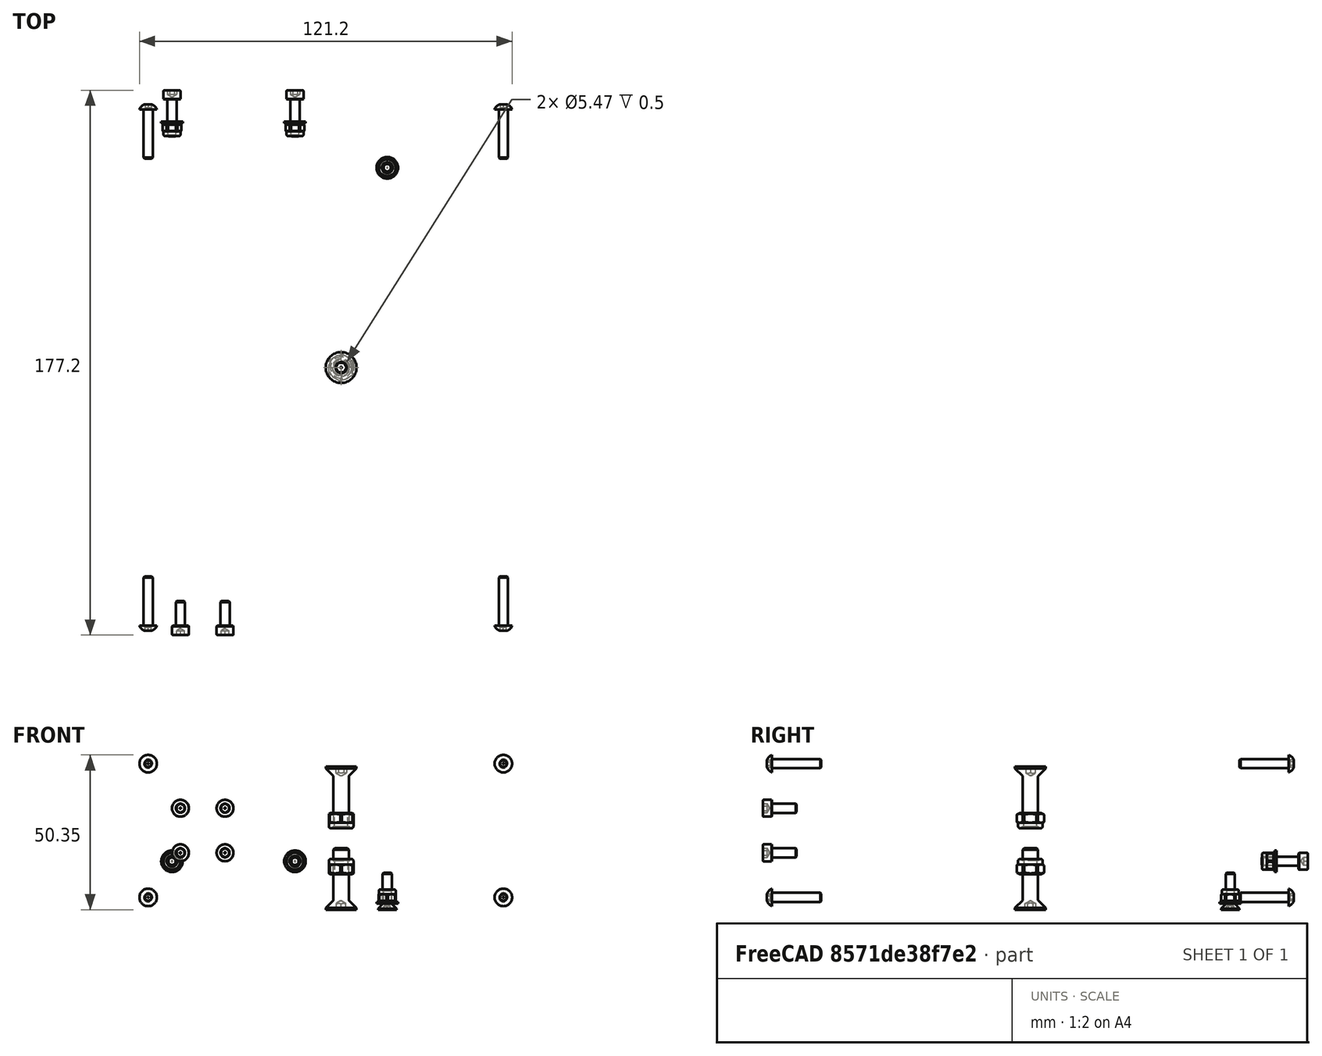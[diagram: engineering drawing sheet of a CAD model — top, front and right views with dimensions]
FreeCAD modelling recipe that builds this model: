
FCSTD DOCUMENT  (FreeCAD 0.20R28730 (Git))
Label: OpenSolder Station
License: All rights reserved
LicenseURL: http://en.wikipedia.org/wiki/All_rights_reserved
objects: Part::FeaturePython×25, TechDraw::DrawViewBalloon×24, App::Link×20, App::DocumentObjectGroup×13, TechDraw::DrawViewDimension×9, PartDesign::CoordinateSystem×7, TechDraw::DrawProjGroupItem×5, Spreadsheet::Sheet×4, TechDraw::DrawSVGTemplate×4, TechDraw::DrawPage×4, Sketcher::SketchObject×3, TechDraw::DrawProjGroup×2, TechDraw::DrawViewPart×2, App::FeaturePython×1, App::Part×1, TechDraw::DrawViewSpreadsheet×1, TechDraw::DrawViewSection×1
note: 35 computed .brp shape members not serialized (recipe doc carries the construction recipe); baked Part::Feature solids carry a one-line shape summary decoded from their .brp
EXTERNAL_REF file=Parts/Enclosure 1455Q1602BK.FCStd obj=LCS_Extrusion
EXTERNAL_REF file=Parts/Enclosure 1455Q1602BK.FCStd obj=Body
EXTERNAL_REF file=Parts/Enclosure 1455Q1602BK.FCStd obj=LCS_Cap
EXTERNAL_REF file=Parts/Enclosure 1455Q1602BK.FCStd obj=Body001
EXTERNAL_REF file=Parts/Enclosure 1455Q1602BK.FCStd obj=LCS_Transformer_Mounting_Hole
EXTERNAL_REF file=Parts/Transformer Spacer.FCStd obj=LCS_Transformer_Spacer_2
EXTERNAL_REF file=Parts/Transformer Spacer.FCStd obj=Body
EXTERNAL_REF file=Parts/Enclosure 1455Q1602BK.FCStd obj=LCS_Transformer_Outside_Mounting_Hole
EXTERNAL_REF file=Parts/Transformer Spacer.FCStd obj=LCS_Transformer_Spacer_Nut_Bottom
EXTERNAL_REF file=Parts/Transformer Spacer.FCStd obj=LCS_Transformer_Spacer_Nut_Top
EXTERNAL_REF file=Parts/Transformer.FCStd obj=LCS_Foam_Bottom
EXTERNAL_REF file=Parts/Transformer.FCStd obj=Body001
EXTERNAL_REF file=Parts/Transformer.FCStd obj=LCS_Foam_Top
EXTERNAL_REF file=Parts/Transformer.FCStd obj=LCS_Transformer_Bottom
EXTERNAL_REF file=Parts/Transformer.FCStd obj=Body
EXTERNAL_REF file=Parts/Transformer.FCStd obj=LCS_Transformer_Top
EXTERNAL_REF file=Parts/Transformer.FCStd obj=LCS_Transformer_Washer_Plane
EXTERNAL_REF file=Parts/Transformer.FCStd obj=Body002
EXTERNAL_REF file=Parts/Transformer.FCStd obj=LCS_Transformer_Washer_Screw_Top
EXTERNAL_REF file=Parts/Panels.FCStd obj=LCS_Front_Hole_1_Bottom
EXTERNAL_REF file=Parts/Panels.FCStd obj=Body
EXTERNAL_REF file=Parts/Panels.FCStd obj=LCS_Rear_Hole_1_Bottom
EXTERNAL_REF file=Parts/Panels.FCStd obj=Body001
EXTERNAL_REF file=Parts/PCB.FCStd obj=LCS_PCBA
EXTERNAL_REF file=Parts/Panels.FCStd obj=LCS_PCBA_Mount
EXTERNAL_REF file=Parts/PCB.FCStd obj=openSolderV0_2_1
EXTERNAL_REF file=Parts/Connector Minijack MJ-064H.FCStd obj=LCS_1
EXTERNAL_REF file=Parts/Panels.FCStd obj=LCS_Rear_Holder_Connector
EXTERNAL_REF file=Parts/Connector Minijack MJ-064H.FCStd obj=Body
EXTERNAL_REF file=Parts/Panels.FCStd obj=LCS_Rear_STlink_Connector
EXTERNAL_REF file=Parts/Connector IEC-C14 703W-0004.FCStd obj=LCS_IEC_Connector
EXTERNAL_REF file=Parts/Panels.FCStd obj=LCS_Rear_IDC_Connector
EXTERNAL_REF file=Parts/Connector IEC-C14 703W-0004.FCStd obj=_03W_00____04
EXTERNAL_REF file=Parts/Panels.FCStd obj=LCS_Rear_Switch
EXTERNAL_REF file=Parts/Rocker Switch CWSB11AA2F.FCStd obj=LCS_Switch
EXTERNAL_REF file=Parts/Rocker Switch CWSB11AA2F.FCStd obj=CWSB11AA2F
EXTERNAL_REF file=Parts/Rotary Encoder Knob.FCStd obj=LCS_Knob
EXTERNAL_REF file=Parts/Rotary Encoder Knob.FCStd obj=Body
EXTERNAL_REF file=Parts/Panels.FCStd obj=LCS_Front_Connector_Hole_1
EXTERNAL_REF file=Parts/Panels.FCStd obj=LCS_Front_Connector_Hole_2
EXTERNAL_REF file=Parts/Panels.FCStd obj=LCS_Front_Connector_Hole_3
EXTERNAL_REF file=Parts/Panels.FCStd obj=LCS_Front_Connector_Hole_4
EXTERNAL_REF file=Parts/Panels.FCStd obj=LCS_Front_Hole_1_Top
EXTERNAL_REF file=Parts/Panels.FCStd obj=LCS_Front_Hole_2_Top
EXTERNAL_REF file=Parts/Panels.FCStd obj=LCS_Front_Hole_3_Top
EXTERNAL_REF file=Parts/Panels.FCStd obj=LCS_Front_Hole_4_Top
EXTERNAL_REF file=Parts/Panels.FCStd obj=LCS_Rear_Hole_4_Top
EXTERNAL_REF file=Parts/Panels.FCStd obj=LCS_Rear_Hole_1_Top
EXTERNAL_REF file=Parts/Panels.FCStd obj=LCS_Rear_Hole_2_Top
EXTERNAL_REF file=Parts/Panels.FCStd obj=LCS_Rear_Hole_3_Top
EXTERNAL_REF file=Parts/Enclosure 1455Q1602BK.FCStd obj=LCS_Outside_Grounding_Hole
EXTERNAL_REF file=Parts/Connector IEC-C14 703W-0004.FCStd obj=LCS_IEC_Hole_1
EXTERNAL_REF file=Parts/Connector IEC-C14 703W-0004.FCStd obj=LCS_IEC_Hole_2
EXTERNAL_REF file=Parts/Enclosure 1455Q1602BK.FCStd obj=LCS_Grounding_Hole
EXTERNAL_REF file=Parts/Rubber Pad.FCStd obj=LCS_1
EXTERNAL_REF file=Parts/Rubber Pad.FCStd obj=Body
EXTERNAL_REF file=Parts/Fuse Holder Inline.FCStd obj=LCS_0
EXTERNAL_REF file=Parts/Fuse Holder Inline.FCStd obj=Fuse_Holder_01500274ZXU

FEATURE [PartDesign::CoordinateSystem] LCS_Origin
  AttacherType = Attacher::AttachEngine3D
  MapMode = 2
  Support = -> [X_Axis]
FEATURE [App::FeaturePython] Variables  # WARN: FeaturePython — macro-defined, semantics opaque (R4)
  Type = App::PropertyContainer
FEATURE [App::DocumentObjectGroup] Constraints
FEATURE [App::Link] _455Q1602BK_Extrusion  label="Enclosure_1455Q1602BK_Extrusion"
  AssemblyType = Part::Link
  AttachedBy = #LCS_Extrusion
  AttachedTo = Parent Assembly#LCS_Origin
  AttachmentOffset = pos=(0,0,0) rot=(-1,0,0;1.5708rad)
  LinkPlacement = pos=(0,0,0) rot=(-1,0,0;1.5708rad)
  LinkedObject = -> <external Parts/Enclosure 1455Q1602BK.FCStd>#Body
  Placement = pos=(0,0,0) rot=(-1,0,0;1.5708rad)
  SolverId = Asm4EE
  expr: Placement = LCS_Origin.Placement * AttachmentOffset * Enclosure_1455Q1602BK#LCS_Extrusion.Placement ^ -1
FEATURE [App::Link] _455Q1602BK_Cap  label="Enclosure_1455Q1602BK_Cap"
  AssemblyType = Part::Link
  AttachedBy = #LCS_Cap
  AttachedTo = _455Q1602BK_Extrusion#LCS_Extrusion
  LinkPlacement = pos=(0,2.29e-14,51.5) rot=(-1,0,0;1.5708rad)
  LinkedObject = -> <external Parts/Enclosure 1455Q1602BK.FCStd>#Body001
  Placement = pos=(0,2.29e-14,51.5) rot=(-1,0,0;1.5708rad)
  SolverId = Asm4EE
  expr: Placement = _455Q1602BK_Extrusion.Placement * Enclosure_1455Q1602BK#LCS_Extrusion.Placement * AttachmentOffset * Enclosure_1455Q1602BK#LCS_Cap.Placement ^ -1
FEATURE [App::Link] Transformer_Spacer
  AssemblyType = Part::Link
  AttachedBy = #LCS_Transformer_Spacer_2
  AttachedTo = _455Q1602BK_Extrusion#LCS_Transformer_Mounting_Hole
  AttachmentOffset = pos=(0,0,0) rot=(0,0,-1;1.5708rad)
  LinkPlacement = pos=(5,1.2e-14,21.5) rot=(0,0,-1;1.5708rad)
  LinkedObject = -> <external Parts/Transformer Spacer.FCStd>#Body
  Placement = pos=(5,1.2e-14,21.5) rot=(0,0,-1;1.5708rad)
  SolverId = Asm4EE
  expr: Placement = _455Q1602BK_Extrusion.Placement * Enclosure_1455Q1602BK#LCS_Transformer_Mounting_Hole.Placement * AttachmentOffset * Transformer_Spacer#LCS_Transformer_Spacer_2.Placement ^ -1
FEATURE [Part::FeaturePython] Screw  label="M5x20-Screw"  # Fasteners workbench fastener (typed FeaturePython)
  AssemblyType = Part::Link
  AttachedBy = Origin
  AttachedTo = _455Q1602BK_Extrusion#LCS_Transformer_Outside_Mounting_Hole
  Placement = pos=(5,0,0) rot=(0.707107,-0.707107,0;3.14159rad)
  SolverId = Asm4EE
  diameter = 5
  invert = false
  length = 4
  lengthCustom = 20
  matchOuter = false
  offset = 0
  thread = false
  type = 18
  expr: Placement = _455Q1602BK_Extrusion.Placement * Enclosure_1455Q1602BK#LCS_Transformer_Outside_Mounting_Hole.Placement * AttachmentOffset
FEATURE [Part::FeaturePython] Nut  label="M5-Nut001"  # Fasteners workbench fastener (typed FeaturePython)
  AssemblyType = Part::Link
  AttachedBy = Origin
  AttachedTo = Transformer_Spacer#LCS_Transformer_Spacer_Nut_Bottom
  AttachmentOffset = pos=(0,0,0) rot=(0,0,1;1.5708rad)
  Placement = pos=(5,6.5e-15,11.5) rot=(0,0,1;1.5708rad)
  SolverId = Asm4EE
  diameter = 3
  invert = false
  matchOuter = false
  offset = 0
  thread = false
  type = 5
  expr: Placement = Transformer_Spacer.Placement * Transformer_Spacer#LCS_Transformer_Spacer_Nut_Bottom.Placement * AttachmentOffset
FEATURE [Part::FeaturePython] Nut001  label="M5-Nut"  # Fasteners workbench fastener (typed FeaturePython)
  AssemblyType = Part::Link
  AttachedBy = Origin
  AttachedTo = Transformer_Spacer#LCS_Transformer_Spacer_Nut_Top
  AttachmentOffset = pos=(0,0,0) rot=(0.707107,-0.707107,0;3.14159rad)
  Placement = pos=(5,1.75e-14,31.5) rot=(0.707107,-0.707107,0;3.14159rad)
  SolverId = Asm4EE
  diameter = 3
  invert = false
  matchOuter = false
  offset = 0
  thread = false
  type = 5
  expr: Placement = Transformer_Spacer.Placement * Transformer_Spacer#LCS_Transformer_Spacer_Nut_Top.Placement * AttachmentOffset
FEATURE [App::Link] Foam_Bottom
  AssemblyType = Part::Link
  AttachedBy = #LCS_Foam_Bottom
  AttachedTo = _455Q1602BK_Extrusion#LCS_Transformer_Mounting_Hole
  AttachmentOffset = pos=(0,0,0) rot=(1,0,0;3.14159rad)
  LinkPlacement = pos=(5,1.3e-15,2) rot=(0,0,1;3.14159rad)
  LinkedObject = -> <external Parts/Transformer.FCStd>#Body001
  Placement = pos=(5,1.3e-15,2) rot=(0,0,1;3.14159rad)
  SolverId = Asm4EE
  expr: Placement = _455Q1602BK_Extrusion.Placement * Enclosure_1455Q1602BK#LCS_Transformer_Mounting_Hole.Placement * AttachmentOffset * Transformer#LCS_Foam_Bottom.Placement ^ -1
FEATURE [App::Link] Transformer
  AssemblyType = Part::Link
  AttachedBy = #LCS_Transformer_Bottom
  AttachedTo = Foam_Bottom#LCS_Foam_Top
  AttachmentOffset = pos=(0,0,0) rot=(0,0,-1;1.5708rad)
  LinkPlacement = pos=(5,-2.2e-15,2) rot=(0,0,1;4.71239rad)
  LinkedObject = -> <external Parts/Transformer.FCStd>#Body
  Placement = pos=(5,-2.2e-15,2) rot=(0,0,1;4.71239rad)
  SolverId = Asm4EE
  expr: Placement = Foam_Bottom.Placement * Transformer#LCS_Foam_Top.Placement * AttachmentOffset * Transformer#LCS_Transformer_Bottom.Placement ^ -1
FEATURE [App::Link] Foam_Top
  AssemblyType = Part::Link
  AttachedBy = #LCS_Foam_Bottom
  AttachedTo = Transformer#LCS_Transformer_Top
  LinkPlacement = pos=(5,2.42e-14,47.5) rot=(0,0,1;4.71239rad)
  LinkedObject = -> <external Parts/Transformer.FCStd>#Body001
  Placement = pos=(5,2.42e-14,47.5) rot=(0,0,1;4.71239rad)
  SolverId = Asm4EE
  expr: Placement = Transformer.Placement * Transformer#LCS_Transformer_Top.Placement * AttachmentOffset * Transformer#LCS_Foam_Bottom.Placement ^ -1
FEATURE [App::Link] Transformer_Washer
  AssemblyType = Part::Link
  AttachedBy = #LCS_Transformer_Washer_Plane
  AttachedTo = Foam_Top#LCS_Foam_Top
  LinkPlacement = pos=(5,2.29e-14,43) rot=(0,0,1;4.71239rad)
  LinkedObject = -> <external Parts/Transformer.FCStd>#Body002
  Placement = pos=(5,2.29e-14,43) rot=(0,0,1;4.71239rad)
  SolverId = Asm4EE
  expr: Placement = Foam_Top.Placement * Transformer#LCS_Foam_Top.Placement * AttachmentOffset * Transformer#LCS_Transformer_Washer_Plane.Placement ^ -1
FEATURE [App::DocumentObjectGroup] Transformer_Group
  Group = -> [Foam_Bottom,Transformer,Foam_Top,Transformer_Washer]
FEATURE [Part::FeaturePython] Screw001  label="M5x20-Screw001"  # Fasteners workbench fastener (typed FeaturePython)
  AssemblyType = Part::Link
  AttachedBy = Origin
  AttachedTo = Transformer_Washer#LCS_Transformer_Washer_Screw_Top
  AttachmentOffset = pos=(0,0,-2) rot=(1,0,0;3.14159rad)
  Placement = pos=(5,2.37e-14,46.5) rot=(0,0,-1;3.14159rad)
  SolverId = Asm4EE
  diameter = 5
  invert = false
  length = 4
  lengthCustom = 20
  matchOuter = false
  offset = 0
  thread = false
  type = 18
  expr: Placement = Transformer_Washer.Placement * Transformer#LCS_Transformer_Washer_Screw_Top.Placement * AttachmentOffset
FEATURE [App::DocumentObjectGroup] Transformer_Fasteners
  Group = -> [Screw,Screw001,Nut001,Nut]
FEATURE [Sketcher::SketchObject] Front_Panel_Sketch
  AttachmentOffset = pos=(0,0,80) rot=(0,0,1;0rad)
  FullyConstrained = true
  MapMode = 5
  Placement = pos=(0,-80,-1.78e-14) rot=(1,0,0;1.5708rad)
  Support = -> [XZ_Plane]
  sketch-geometry (8):
    g0: LineSegment StartX=-57.75 StartY=47.5 StartZ=0 EndX=57.75 EndY=47.5 EndZ=0
    g1: LineSegment StartX=57.75 StartY=47.5 StartZ=0 EndX=57.75 EndY=4 EndZ=0
    g2: LineSegment StartX=57.75 StartY=4 StartZ=0 EndX=-57.75 EndY=4 EndZ=0
    g3: LineSegment StartX=-57.75 StartY=4 StartZ=0 EndX=-57.75 EndY=47.5 EndZ=0
    g4: Circle CenterX=-57.75 CenterY=47.5 CenterZ=0 NormalX=0 NormalY=0 NormalZ=1 AngleXU=0 Radius=1.75
    g5: Circle CenterX=57.75 CenterY=47.5 CenterZ=0 NormalX=0 NormalY=0 NormalZ=1 AngleXU=0 Radius=1.75
    g6: Circle CenterX=57.75 CenterY=4 CenterZ=0 NormalX=0 NormalY=0 NormalZ=1 AngleXU=0 Radius=1.75
    g7: Circle CenterX=-57.75 CenterY=4 CenterZ=0 NormalX=0 NormalY=0 NormalZ=1 AngleXU=0 Radius=1.75
  constraints (19):
    c: Coincident(g0,g1)
    c: Coincident(g1,g2)
    c: Coincident(g2,g3)
    c: Coincident(g3,g0)
    c: Horizontal(g0)
    c: Vertical(g1)
    c: Vertical(g3)
    c: Symmetric(g2,g1,g-2)
    c: DistanceX(g2,g2) = 115.5
    c: DistanceY(g3,g3) = 43.5
    c: DistanceY(g-1,g2) = 4
    c: Coincident(g4,g0)
    c: Coincident(g5,g0)
    c: Coincident(g6,g1)
    c: Coincident(g7,g2)
    c: Equal(g7,g4)
    c: Equal(g7,g5)
    c: Equal(g7,g6)
    c: Diameter(g7) = 3.5
FEATURE [Sketcher::SketchObject] Front_Panel_Sketch001  label="Rear_Panel_Sketch"
  AttachmentOffset = pos=(0,0,-80) rot=(0,0,1;0rad)
  FullyConstrained = true
  MapMode = 5
  Placement = pos=(0,80,1.78e-14) rot=(1,0,0;1.5708rad)
  Support = -> [XZ_Plane]
  sketch-geometry (8):
    g0: LineSegment StartX=-57.75 StartY=47.5 StartZ=0 EndX=57.75 EndY=47.5 EndZ=0
    g1: LineSegment StartX=57.75 StartY=47.5 StartZ=0 EndX=57.75 EndY=4 EndZ=0
    g2: LineSegment StartX=57.75 StartY=4 StartZ=0 EndX=-57.75 EndY=4 EndZ=0
    g3: LineSegment StartX=-57.75 StartY=4 StartZ=0 EndX=-57.75 EndY=47.5 EndZ=0
    g4: Circle CenterX=-57.75 CenterY=47.5 CenterZ=0 NormalX=0 NormalY=0 NormalZ=1 AngleXU=0 Radius=1.75
    g5: Circle CenterX=57.75 CenterY=47.5 CenterZ=0 NormalX=0 NormalY=0 NormalZ=1 AngleXU=0 Radius=1.75
    g6: Circle CenterX=57.75 CenterY=4 CenterZ=0 NormalX=0 NormalY=0 NormalZ=1 AngleXU=0 Radius=1.75
    g7: Circle CenterX=-57.75 CenterY=4 CenterZ=0 NormalX=0 NormalY=0 NormalZ=1 AngleXU=0 Radius=1.75
  constraints (19):
    c: Coincident(g0,g1)
    c: Coincident(g1,g2)
    c: Coincident(g2,g3)
    c: Coincident(g3,g0)
    c: Horizontal(g0)
    c: Vertical(g1)
    c: Vertical(g3)
    c: Symmetric(g2,g1,g-2)
    c: DistanceX(g2,g2) = 115.5
    c: DistanceY(g3,g3) = 43.5
    c: DistanceY(g-1,g2) = 4
    c: Coincident(g4,g0)
    c: Coincident(g5,g0)
    c: Coincident(g6,g1)
    c: Coincident(g7,g2)
    c: Equal(g7,g4)
    c: Equal(g7,g5)
    c: Equal(g7,g6)
    c: Diameter(g7) = 3.5
FEATURE [PartDesign::CoordinateSystem] LCS_Assembly_Front_Hole
  AttacherType = Attacher::AttachEngine3D
  MapMode = 11
  Placement = pos=(-57.75,-80,47.5) rot=(0.57735,-0.57735,0.57735;2.0944rad)
  Support = -> [Front_Panel_Sketch]
FEATURE [PartDesign::CoordinateSystem] LCS_Assembly_Rear_Hole
  AttacherType = Attacher::AttachEngine3D
  MapMode = 11
  Placement = pos=(57.75,80,47.5) rot=(0.57735,-0.57735,0.57735;2.0944rad)
  Support = -> [Front_Panel_Sketch001]
FEATURE [App::Link] Front_Panel
  AssemblyType = Part::Link
  AttachedBy = #LCS_Front_Hole_1_Bottom
  AttachedTo = Parent Assembly#LCS_Assembly_Front_Hole
  LinkPlacement = pos=(0,-80,25.75) rot=(0,0,1;0rad)
  LinkedObject = -> <external Parts/Panels.FCStd>#Body
  Placement = pos=(0,-80,25.75) rot=(0,0,1;0rad)
  SolverId = Asm4EE
  expr: Placement = LCS_Assembly_Front_Hole.Placement * AttachmentOffset * Panels#LCS_Front_Hole_1_Bottom.Placement ^ -1
FEATURE [App::Link] Rear_Panel
  AssemblyType = Part::Link
  AttachedBy = #LCS_Rear_Hole_1_Bottom
  AttachedTo = Parent Assembly#LCS_Assembly_Rear_Hole
  AttachmentOffset = pos=(0,0,0) rot=(1,0,0;3.14159rad)
  LinkPlacement = pos=(-7.1e-15,80,25.75) rot=(0,0,1;3.14159rad)
  LinkedObject = -> <external Parts/Panels.FCStd>#Body001
  Placement = pos=(-7.1e-15,80,25.75) rot=(0,0,1;3.14159rad)
  SolverId = Asm4EE
  expr: Placement = LCS_Assembly_Rear_Hole.Placement * AttachmentOffset * Panels#LCS_Rear_Hole_1_Bottom.Placement ^ -1
FEATURE [App::Link] openSolderV0_2_PCBA  label="openSolderV0.2_PCBA"
  AssemblyType = Part::Link
  AttachedBy = #LCS_PCBA
  AttachedTo = Front_Panel#LCS_PCBA_Mount
  AttachmentOffset = pos=(0,0,0) rot=(1,0,0;3.14159rad)
  LinkPlacement = pos=(0,-73,25.75) rot=(0,0.707107,0.707107;3.14159rad)
  LinkedObject = -> <external Parts/PCB.FCStd>#openSolderV0_2_1
  Placement = pos=(0,-73,25.75) rot=(0,0.707107,0.707107;3.14159rad)
  SolverId = Asm4EE
  expr: Placement = Front_Panel.Placement * Panels#LCS_PCBA_Mount.Placement * AttachmentOffset * PCB#LCS_PCBA.Placement ^ -1
FEATURE [App::Link] Connector_Holder
  AssemblyType = Part::Link
  AttachedBy = #LCS_1
  AttachedTo = Rear_Panel#LCS_Rear_Holder_Connector
  AttachmentOffset = pos=(0,0,0) rot=(0,0,1;1.5708rad)
  LinkPlacement = pos=(47.5,84,10.75) rot=(0,0,1;4.71239rad)
  LinkedObject = -> <external Parts/Connector Minijack MJ-064H.FCStd>#Body
  Placement = pos=(47.5,84,10.75) rot=(0,0,1;4.71239rad)
  SolverId = Asm4EE
  expr: Placement = Rear_Panel.Placement * Panels#LCS_Rear_Holder_Connector.Placement * AttachmentOffset * Connector_Minijack_MJ_064H#LCS_1.Placement ^ -1
FEATURE [App::Link] Connector_STlink
  AssemblyType = Part::Link
  AttachedBy = #LCS_1
  AttachedTo = Rear_Panel#LCS_Rear_STlink_Connector
  AttachmentOffset = pos=(0,0,0) rot=(0,0,1;1.5708rad)
  LinkPlacement = pos=(47.5,84,40.75) rot=(0,0,1;4.71239rad)
  LinkedObject = -> <external Parts/Connector Minijack MJ-064H.FCStd>#Body
  Placement = pos=(47.5,84,40.75) rot=(0,0,1;4.71239rad)
  SolverId = Asm4EE
  expr: Placement = Rear_Panel.Placement * Panels#LCS_Rear_STlink_Connector.Placement * AttachmentOffset * Connector_Minijack_MJ_064H#LCS_1.Placement ^ -1
FEATURE [App::Link] _03W_00_IEC_C14_Connector  label="Connector_IEC-C14_703W-0004"
  AssemblyType = Part::Link
  AttachedBy = #LCS_IEC_Connector
  AttachedTo = Rear_Panel#LCS_Rear_IDC_Connector
  AttachmentOffset = pos=(0,0,0) rot=(0,0,1;1.5708rad)
  LinkPlacement = pos=(-27.5841,83.3477,15.75) rot=(0,1,0;3.14159rad)
  LinkedObject = -> <external Parts/Connector IEC-C14 703W-0004.FCStd>#_03W_00____04
  Placement = pos=(-27.5841,83.3477,15.75) rot=(0,1,0;3.14159rad)
  SolverId = Asm4EE
  expr: Placement = Rear_Panel.Placement * Panels#LCS_Rear_IDC_Connector.Placement * AttachmentOffset * Connector_IEC_C14_703W_0004#LCS_IEC_Connector.Placement ^ -1
FEATURE [App::Link] CWSB11AA2F_Switch  label="Rocker_Switch_CWSB11AA2F"
  AssemblyType = Part::Link
  AttachedBy = #LCS_Switch
  AttachedTo = Rear_Panel#LCS_Rear_Switch
  AttachmentOffset = pos=(0,0,0) rot=(1,0,0;3.14159rad)
  LinkPlacement = pos=(-30,84,38.75) rot=(0,1,0;4.71239rad)
  LinkedObject = -> <external Parts/Rocker Switch CWSB11AA2F.FCStd>#CWSB11AA2F
  Placement = pos=(-30,84,38.75) rot=(0,1,0;4.71239rad)
  SolverId = Asm4EE
  expr: Placement = Rear_Panel.Placement * Panels#LCS_Rear_Switch.Placement * AttachmentOffset * Rocker_Switch_CWSB11AA2F#LCS_Switch.Placement ^ -1
FEATURE [App::Link] Knob  label="Rotary_Encoder_Knob"
  AssemblyType = Part::Link
  AttachedBy = #LCS_Knob
  AttachedTo = Front_Panel#LCS_PCBA_Mount
  AttachmentOffset = pos=(0,0,5) rot=(0,0,1;1.5708rad)
  LinkPlacement = pos=(40,-85,25.75) rot=(0.57735,-0.57735,0.57735;2.0944rad)
  LinkedObject = -> <external Parts/Rotary Encoder Knob.FCStd>#Body
  Placement = pos=(40,-85,25.75) rot=(0.57735,-0.57735,0.57735;2.0944rad)
  SolverId = Asm4EE
  expr: Placement = Front_Panel.Placement * Panels#LCS_PCBA_Mount.Placement * AttachmentOffset * Rotary_Encoder_Knob#LCS_Knob.Placement ^ -1
FEATURE [Part::FeaturePython] Screw002  label="M3x8-Screw"  # Fasteners workbench fastener (typed FeaturePython)
  AssemblyType = Part::Link
  AttachedBy = Origin
  AttachedTo = Front_Panel#LCS_Front_Connector_Hole_1
  Placement = pos=(-47.25,-84,33) rot=(0.57735,-0.57735,0.57735;2.0944rad)
  SolverId = Asm4EE
  diameter = 4
  invert = false
  length = 2
  lengthCustom = 8
  matchOuter = false
  offset = 0
  thread = false
  type = 34
  expr: Placement = Front_Panel.Placement * Panels#LCS_Front_Connector_Hole_1.Placement * AttachmentOffset
FEATURE [Part::FeaturePython] Screw003  label="M3x8-Screw145"  # Fasteners workbench fastener (typed FeaturePython)
  AssemblyType = Part::Link
  AttachedBy = Origin
  AttachedTo = Front_Panel#LCS_Front_Connector_Hole_2
  Placement = pos=(-32.75,-84,33) rot=(0.57735,-0.57735,0.57735;2.0944rad)
  SolverId = Asm4EE
  diameter = 4
  invert = false
  length = 2
  lengthCustom = 8
  matchOuter = false
  offset = 0
  thread = false
  type = 34
  expr: Placement = Front_Panel.Placement * Panels#LCS_Front_Connector_Hole_2.Placement * AttachmentOffset
FEATURE [Part::FeaturePython] Screw004  label="M3x8-Screw146"  # Fasteners workbench fastener (typed FeaturePython)
  AssemblyType = Part::Link
  AttachedBy = Origin
  AttachedTo = Front_Panel#LCS_Front_Connector_Hole_3
  Placement = pos=(-32.75,-84,18.5) rot=(0.57735,-0.57735,0.57735;2.0944rad)
  SolverId = Asm4EE
  diameter = 4
  invert = false
  length = 2
  lengthCustom = 8
  matchOuter = false
  offset = 0
  thread = false
  type = 34
  expr: Placement = Front_Panel.Placement * Panels#LCS_Front_Connector_Hole_3.Placement * AttachmentOffset
FEATURE [Part::FeaturePython] Screw005  label="M3x8-Screw147"  # Fasteners workbench fastener (typed FeaturePython)
  AssemblyType = Part::Link
  AttachedBy = Origin
  AttachedTo = Front_Panel#LCS_Front_Connector_Hole_4
  Placement = pos=(-47.25,-84,18.5) rot=(0.57735,-0.57735,0.57735;2.0944rad)
  SolverId = Asm4EE
  diameter = 4
  invert = false
  length = 2
  lengthCustom = 8
  matchOuter = false
  offset = 0
  thread = false
  type = 34
  expr: Placement = Front_Panel.Placement * Panels#LCS_Front_Connector_Hole_4.Placement * AttachmentOffset
FEATURE [Part::FeaturePython] Screw006  label="M3x16-Screw"  # Fasteners workbench fastener (typed FeaturePython)
  AssemblyType = Part::Link
  AttachedBy = Origin
  AttachedTo = Front_Panel#LCS_Front_Hole_1_Top
  Placement = pos=(-57.75,-84,47.5) rot=(0.57735,-0.57735,0.57735;2.0944rad)
  SolverId = Asm4EE
  diameter = 1
  invert = false
  length = 5
  lengthCustom = 16
  matchOuter = false
  offset = 0
  thread = false
  type = 40
  expr: Placement = Front_Panel.Placement * Panels#LCS_Front_Hole_1_Top.Placement * AttachmentOffset
FEATURE [Part::FeaturePython] Screw007  label="M3x16-Screw043"  # Fasteners workbench fastener (typed FeaturePython)
  AssemblyType = Part::Link
  AttachedBy = Origin
  AttachedTo = Front_Panel#LCS_Front_Hole_2_Top
  Placement = pos=(57.75,-84,47.5) rot=(0.57735,-0.57735,0.57735;2.0944rad)
  SolverId = Asm4EE
  diameter = 1
  invert = false
  length = 5
  lengthCustom = 16
  matchOuter = false
  offset = 0
  thread = false
  type = 40
  expr: Placement = Front_Panel.Placement * Panels#LCS_Front_Hole_2_Top.Placement * AttachmentOffset
FEATURE [Part::FeaturePython] Screw008  label="M3x16-Screw044"  # Fasteners workbench fastener (typed FeaturePython)
  AssemblyType = Part::Link
  AttachedBy = Origin
  AttachedTo = Front_Panel#LCS_Front_Hole_3_Top
  Placement = pos=(57.75,-84,4) rot=(0.57735,-0.57735,0.57735;2.0944rad)
  SolverId = Asm4EE
  diameter = 1
  invert = false
  length = 5
  lengthCustom = 16
  matchOuter = false
  offset = 0
  thread = false
  type = 40
  expr: Placement = Front_Panel.Placement * Panels#LCS_Front_Hole_3_Top.Placement * AttachmentOffset
FEATURE [Part::FeaturePython] Screw009  label="M3x16-Screw045"  # Fasteners workbench fastener (typed FeaturePython)
  AssemblyType = Part::Link
  AttachedBy = Origin
  AttachedTo = Front_Panel#LCS_Front_Hole_4_Top
  Placement = pos=(-57.75,-84,4) rot=(0.57735,-0.57735,0.57735;2.0944rad)
  SolverId = Asm4EE
  diameter = 1
  invert = false
  length = 5
  lengthCustom = 16
  matchOuter = false
  offset = 0
  thread = false
  type = 40
  expr: Placement = Front_Panel.Placement * Panels#LCS_Front_Hole_4_Top.Placement * AttachmentOffset
FEATURE [Part::FeaturePython] Screw010  label="M3x16-Screw049"  # Fasteners workbench fastener (typed FeaturePython)
  AssemblyType = Part::Link
  AttachedBy = Origin
  AttachedTo = Rear_Panel#LCS_Rear_Hole_4_Top
  Placement = pos=(57.75,84,4) rot=(0.57735,0.57735,0.57735;4.18879rad)
  SolverId = Asm4EE
  diameter = 1
  invert = false
  length = 5
  lengthCustom = 16
  matchOuter = false
  offset = 0
  thread = false
  type = 40
  expr: Placement = Rear_Panel.Placement * Panels#LCS_Rear_Hole_4_Top.Placement * AttachmentOffset
FEATURE [Part::FeaturePython] Screw011  label="M3x16-Screw046"  # Fasteners workbench fastener (typed FeaturePython)
  AssemblyType = Part::Link
  AttachedBy = Origin
  AttachedTo = Rear_Panel#LCS_Rear_Hole_1_Top
  Placement = pos=(57.75,84,47.5) rot=(0.57735,0.57735,0.57735;4.18879rad)
  SolverId = Asm4EE
  diameter = 1
  invert = false
  length = 5
  lengthCustom = 16
  matchOuter = false
  offset = 0
  thread = false
  type = 40
  expr: Placement = Rear_Panel.Placement * Panels#LCS_Rear_Hole_1_Top.Placement * AttachmentOffset
FEATURE [Part::FeaturePython] Screw012  label="M3x16-Screw047"  # Fasteners workbench fastener (typed FeaturePython)
  AssemblyType = Part::Link
  AttachedBy = Origin
  AttachedTo = Rear_Panel#LCS_Rear_Hole_2_Top
  Placement = pos=(-57.75,84,47.5) rot=(0.57735,0.57735,0.57735;4.18879rad)
  SolverId = Asm4EE
  diameter = 1
  invert = false
  length = 5
  lengthCustom = 16
  matchOuter = false
  offset = 0
  thread = false
  type = 40
  expr: Placement = Rear_Panel.Placement * Panels#LCS_Rear_Hole_2_Top.Placement * AttachmentOffset
FEATURE [Part::FeaturePython] Screw013  label="M3x16-Screw048"  # Fasteners workbench fastener (typed FeaturePython)
  AssemblyType = Part::Link
  AttachedBy = Origin
  AttachedTo = Rear_Panel#LCS_Rear_Hole_3_Top
  Placement = pos=(-57.75,84,4) rot=(0.57735,0.57735,0.57735;4.18879rad)
  SolverId = Asm4EE
  diameter = 1
  invert = false
  length = 5
  lengthCustom = 16
  matchOuter = false
  offset = 0
  thread = false
  type = 40
  expr: Placement = Rear_Panel.Placement * Panels#LCS_Rear_Hole_3_Top.Placement * AttachmentOffset
FEATURE [App::DocumentObjectGroup] Panel_Fasteners
  Group = -> [Screw006,Screw007,Screw008,Screw009,Screw011,Screw012,Screw013,Screw010]
FEATURE [Part::FeaturePython] Screw016  label="M3x12-Screw090"  # Fasteners workbench fastener (typed FeaturePython)
  AssemblyType = Part::Link
  AttachedBy = Origin
  AttachedTo = _455Q1602BK_Extrusion#LCS_Outside_Grounding_Hole
  Placement = pos=(20,65,-4.29e-14) rot=(0.707107,-0.707107,0;3.14159rad)
  SolverId = Asm4EE
  diameter = 3
  invert = false
  length = 2
  lengthCustom = 12
  matchOuter = false
  offset = 0
  thread = false
  type = 18
  expr: Placement = _455Q1602BK_Extrusion.Placement * Enclosure_1455Q1602BK#LCS_Outside_Grounding_Hole.Placement * AttachmentOffset
FEATURE [Part::FeaturePython] Washer  label="M3-Washer"  # Fasteners workbench fastener (typed FeaturePython)
  AssemblyType = Part::Link
  AttachedBy = Origin
  AttachedTo = _03W_00_IEC_C14_Connector#LCS_IEC_Hole_1
  AttachmentOffset = pos=(0,0,-7.2) rot=(1,0,0;3.14159rad)
  Placement = pos=(-10,80,15.75) rot=(0,0.707107,-0.707107;3.14159rad)
  SolverId = Asm4EE
  diameter = 4
  invert = false
  matchOuter = false
  offset = 0
  type = 3
  expr: Placement = _03W_00_IEC_C14_Connector.Placement * Connector_IEC_C14_703W_0004#LCS_IEC_Hole_1.Placement * AttachmentOffset
FEATURE [Part::FeaturePython] Screw015  label="M3x12-Screw"  # Fasteners workbench fastener (typed FeaturePython)
  AssemblyType = Part::Link
  AttachedBy = Origin
  AttachedTo = _03W_00_IEC_C14_Connector#LCS_IEC_Hole_2
  Placement = pos=(-50,87.2,15.75) rot=(0,0.707107,0.707107;3.14159rad)
  SolverId = Asm4EE
  diameter = 4
  invert = false
  length = 4
  lengthCustom = 12
  matchOuter = false
  offset = 0
  thread = false
  type = 34
  expr: Placement = _03W_00_IEC_C14_Connector.Placement * Connector_IEC_C14_703W_0004#LCS_IEC_Hole_2.Placement * AttachmentOffset
FEATURE [Part::FeaturePython] Screw014  label="M3x12-Screw089"  # Fasteners workbench fastener (typed FeaturePython)
  AssemblyType = Part::Link
  AttachedBy = Origin
  AttachedTo = _03W_00_IEC_C14_Connector#LCS_IEC_Hole_1
  Placement = pos=(-10,87.2,15.75) rot=(0,0.707107,0.707107;3.14159rad)
  SolverId = Asm4EE
  diameter = 4
  invert = false
  length = 4
  lengthCustom = 12
  matchOuter = false
  offset = 0
  thread = false
  type = 34
  expr: Placement = _03W_00_IEC_C14_Connector.Placement * Connector_IEC_C14_703W_0004#LCS_IEC_Hole_1.Placement * AttachmentOffset
FEATURE [Part::FeaturePython] Nut002  label="M3-Nut"  # Fasteners workbench fastener (typed FeaturePython)
  AssemblyType = Part::Link
  AttachedBy = Origin
  AttachedTo = _03W_00_IEC_C14_Connector#LCS_IEC_Hole_1
  AttachmentOffset = pos=(0,0,-7.9) rot=(1,0,0;3.14159rad)
  Placement = pos=(-10,79.3,15.75) rot=(0,0.707107,-0.707107;3.14159rad)
  SolverId = Asm4EE
  diameter = 1
  invert = false
  matchOuter = false
  offset = 0
  thread = false
  type = 5
  expr: Placement = _03W_00_IEC_C14_Connector.Placement * Connector_IEC_C14_703W_0004#LCS_IEC_Hole_1.Placement * AttachmentOffset
FEATURE [App::DocumentObjectGroup] PCBA_Fasteners
  Group = -> [Screw002,Screw003,Screw004,Screw005]
FEATURE [Part::FeaturePython] Washer002  label="M3-Washer084"  # Fasteners workbench fastener (typed FeaturePython)
  AssemblyType = Part::Link
  AttachedBy = Origin
  AttachedTo = _455Q1602BK_Extrusion#LCS_Grounding_Hole
  AttachmentOffset = pos=(0,0,0) rot=(0,0,1;3.14159rad)
  Placement = pos=(20,65,2) rot=(0,0,1;4.71239rad)
  SolverId = Asm4EE
  diameter = 4
  invert = false
  matchOuter = false
  offset = 0
  type = 3
  expr: Placement = _455Q1602BK_Extrusion.Placement * Enclosure_1455Q1602BK#LCS_Grounding_Hole.Placement * AttachmentOffset
FEATURE [Part::FeaturePython] Nut004  label="M3-Nut086"  # Fasteners workbench fastener (typed FeaturePython)
  AssemblyType = Part::Link
  AttachedBy = Origin
  AttachedTo = _455Q1602BK_Extrusion#LCS_Grounding_Hole
  AttachmentOffset = pos=(0,0,0.6) rot=(0,0,1;0rad)
  Placement = pos=(20,65,2.6) rot=(0,0,1;1.5708rad)
  SolverId = Asm4EE
  diameter = 1
  invert = false
  matchOuter = false
  offset = 0
  thread = false
  type = 5
  expr: Placement = _455Q1602BK_Extrusion.Placement * Enclosure_1455Q1602BK#LCS_Grounding_Hole.Placement * AttachmentOffset
FEATURE [App::DocumentObjectGroup] GND_Fasteners
  Group = -> [Screw016,Washer002,Nut004]
FEATURE [Part::FeaturePython] Washer003  label="M3-Washer083"  # Fasteners workbench fastener (typed FeaturePython)
  AssemblyType = Part::Link
  AttachedBy = Origin
  AttachedTo = _03W_00_IEC_C14_Connector#LCS_IEC_Hole_2
  AttachmentOffset = pos=(0,0,-7.2) rot=(1,0,0;3.14159rad)
  Placement = pos=(-50,80,15.75) rot=(0,0.707107,-0.707107;3.14159rad)
  SolverId = Asm4EE
  diameter = 4
  invert = false
  matchOuter = false
  offset = 0
  type = 3
  expr: Placement = _03W_00_IEC_C14_Connector.Placement * Connector_IEC_C14_703W_0004#LCS_IEC_Hole_2.Placement * AttachmentOffset
FEATURE [Part::FeaturePython] Nut005  label="M3-Nut085"  # Fasteners workbench fastener (typed FeaturePython)
  AssemblyType = Part::Link
  AttachedBy = Origin
  AttachedTo = _03W_00_IEC_C14_Connector#LCS_IEC_Hole_2
  AttachmentOffset = pos=(0,0,-7.9) rot=(1,0,0;3.14159rad)
  Placement = pos=(-50,79.3,15.75) rot=(0,0.707107,-0.707107;3.14159rad)
  SolverId = Asm4EE
  diameter = 1
  invert = false
  matchOuter = false
  offset = 0
  thread = false
  type = 5
  expr: Placement = _03W_00_IEC_C14_Connector.Placement * Connector_IEC_C14_703W_0004#LCS_IEC_Hole_2.Placement * AttachmentOffset
FEATURE [App::DocumentObjectGroup] ICD_Fasteners
  Group = -> [Screw015,Screw014,Washer,Washer003,Nut002,Nut005]
FEATURE [App::DocumentObjectGroup] Fasteners
  Group = -> [Transformer_Fasteners,Panel_Fasteners,ICD_Fasteners,PCBA_Fasteners,GND_Fasteners]
FEATURE [Sketcher::SketchObject] Rubber_Pad_Sketch
  FullyConstrained = true
  MapMode = 5
  Support = -> [XY_Plane]
  sketch-geometry (9):
    g0: LineSegment StartX=-42.5 StartY=-67.5 StartZ=0 EndX=-42.5 EndY=67.5 EndZ=0
    g1: LineSegment StartX=-42.5 StartY=67.5 StartZ=0 EndX=42.5 EndY=67.5 EndZ=0
    g2: LineSegment StartX=42.5 StartY=67.5 StartZ=0 EndX=42.5 EndY=-67.5 EndZ=0
    g3: LineSegment StartX=42.5 StartY=-67.5 StartZ=0 EndX=-42.5 EndY=-67.5 EndZ=0
    g4: GeomPoint X=0 Y=0 Z=0
    g5: Circle CenterX=-42.5 CenterY=67.5 CenterZ=0 NormalX=0 NormalY=0 NormalZ=1 AngleXU=0 Radius=10
    g6: Circle CenterX=42.5 CenterY=67.5 CenterZ=0 NormalX=0 NormalY=0 NormalZ=1 AngleXU=0 Radius=10
    g7: Circle CenterX=42.5 CenterY=-67.5 CenterZ=0 NormalX=0 NormalY=0 NormalZ=1 AngleXU=0 Radius=10
    g8: Circle CenterX=-42.5 CenterY=-67.5 CenterZ=0 NormalX=0 NormalY=0 NormalZ=1 AngleXU=0 Radius=10
  constraints (20):
    c: Coincident(g0,g1)
    c: Coincident(g1,g2)
    c: Coincident(g2,g3)
    c: Coincident(g3,g0)
    c: Horizontal(g1)
    c: Horizontal(g3)
    c: Vertical(g0)
    c: Vertical(g2)
    c: Symmetric(g1,g0,g4)
    c: Coincident(g4,g-1)
    c: Coincident(g5,g0)
    c: Coincident(g6,g1)
    c: Coincident(g7,g2)
    c: Coincident(g8,g0)
    c: Equal(g8,g7)
    c: Equal(g8,g6)
    c: Equal(g8,g5)
    c: Diameter(g8) = 20
    c: DistanceX(g1,g1) = 85
    c: DistanceY(g2,g2) = 135
FEATURE [PartDesign::CoordinateSystem] LCS_Rubber_Pad_1
  AttacherType = Attacher::AttachEngine3D
  MapMode = 11
  Placement = pos=(-42.5,-67.5,0) rot=(0,0,1;1.5708rad)
  Support = -> [Rubber_Pad_Sketch]
FEATURE [PartDesign::CoordinateSystem] LCS_Rubber_Pad_2
  AttacherType = Attacher::AttachEngine3D
  MapMode = 11
  Placement = pos=(-42.5,67.5,0) rot=(0,0,1;1.5708rad)
  Support = -> [Rubber_Pad_Sketch]
FEATURE [PartDesign::CoordinateSystem] LCS_Rubber_Pad_3
  AttacherType = Attacher::AttachEngine3D
  MapMode = 11
  Placement = pos=(42.5,67.5,0) rot=(0,0,1;1.5708rad)
  Support = -> [Rubber_Pad_Sketch]
FEATURE [PartDesign::CoordinateSystem] LCS_Rubber_Pad_4
  AttacherType = Attacher::AttachEngine3D
  MapMode = 11
  Placement = pos=(42.5,-67.5,0) rot=(0,0,1;1.5708rad)
  Support = -> [Rubber_Pad_Sketch]
FEATURE [App::DocumentObjectGroup] LCS
  Group = -> [Front_Panel_Sketch,Front_Panel_Sketch001,Rubber_Pad_Sketch,LCS_Assembly_Front_Hole,LCS_Assembly_Rear_Hole,LCS_Rubber_Pad_1,LCS_Rubber_Pad_2,LCS_Rubber_Pad_3,LCS_Rubber_Pad_4]
FEATURE [App::Link] Rubber_Pad_1
  AssemblyType = Part::Link
  AttachedBy = #LCS_1
  AttachedTo = Parent Assembly#LCS_Rubber_Pad_1
  LinkPlacement = pos=(-42.5,-67.5,0) rot=(-0.707107,-0.707107,0;3.14159rad)
  LinkedObject = -> <external Parts/Rubber Pad.FCStd>#Body
  Placement = pos=(-42.5,-67.5,0) rot=(-0.707107,-0.707107,0;3.14159rad)
  SolverId = Asm4EE
  expr: Placement = LCS_Rubber_Pad_1.Placement * AttachmentOffset * Rubber_Pad#LCS_1.Placement ^ -1
FEATURE [App::Link] Rubber_Pad_002  label="Rubber_Pad_2"
  AssemblyType = Part::Link
  AttachedBy = #LCS_1
  AttachedTo = Parent Assembly#LCS_Rubber_Pad_2
  LinkPlacement = pos=(-42.5,67.5,0) rot=(-0.707107,-0.707107,0;3.14159rad)
  LinkedObject = -> <external Parts/Rubber Pad.FCStd>#Body
  Placement = pos=(-42.5,67.5,0) rot=(-0.707107,-0.707107,0;3.14159rad)
  SolverId = Asm4EE
  expr: Placement = LCS_Rubber_Pad_2.Placement * AttachmentOffset * Rubber_Pad#LCS_1.Placement ^ -1
FEATURE [App::Link] Rubber_Pad_003  label="Rubber_Pad_3"
  AssemblyType = Part::Link
  AttachedBy = #LCS_1
  AttachedTo = Parent Assembly#LCS_Rubber_Pad_3
  LinkPlacement = pos=(42.5,67.5,0) rot=(-0.707107,-0.707107,0;3.14159rad)
  LinkedObject = -> <external Parts/Rubber Pad.FCStd>#Body
  Placement = pos=(42.5,67.5,0) rot=(-0.707107,-0.707107,0;3.14159rad)
  SolverId = Asm4EE
  expr: Placement = LCS_Rubber_Pad_3.Placement * AttachmentOffset * Rubber_Pad#LCS_1.Placement ^ -1
FEATURE [App::Link] Rubber_Pad_004  label="Rubber_Pad_4"
  AssemblyType = Part::Link
  AttachedBy = #LCS_1
  AttachedTo = Parent Assembly#LCS_Rubber_Pad_4
  LinkPlacement = pos=(42.5,-67.5,0) rot=(-0.707107,-0.707107,0;3.14159rad)
  LinkedObject = -> <external Parts/Rubber Pad.FCStd>#Body
  Placement = pos=(42.5,-67.5,0) rot=(-0.707107,-0.707107,0;3.14159rad)
  SolverId = Asm4EE
  expr: Placement = LCS_Rubber_Pad_4.Placement * AttachmentOffset * Rubber_Pad#LCS_1.Placement ^ -1
FEATURE [App::DocumentObjectGroup] Rubber_Pads
  Group = -> [Rubber_Pad_1,Rubber_Pad_002,Rubber_Pad_003,Rubber_Pad_004]
FEATURE [Spreadsheet::Sheet] Default
  cells = A1=Asm4::ConfigurationTable; A2=0; A4=ObjectName; B4=Visible; C4=Assembly Type; D4=Pos. X; E4=Pos. Y; F4=Pos. Z; G4=Rot. Yaw; H4=Rot. Pitch; I4=Rot. Roll; A5(AssemblyFuse_Holder_01500274ZXU)=Assembly.Fuse_Holder_01500274ZXU; B5=True; C5=Asm4EE; D5=-52; E5=-10; F5=22; G5=0; H5=90; I5=180; A6(AssemblyNut004)=Assembly.Nut004; B6=True; C6=Asm4EE; D6=0; E6=0; F6=0.6; G6=0; H6=0; I6=0; A7(AssemblyWasher002)=Assembly.Washer002; B7=True; C7=Asm4EE; D7=0; E7=0; F7=0; G7=180; H7=2.291831180523293e-14; I7=2.291831180523293e-14; A8(AssemblyScrew016)=Assembly.Screw016; B8=True; C8=Asm4EE; D8=0; E8=0; F8=0; G8=0; H8=0; I8=0; A9(AssemblyScrew005)=Assembly.Screw005; B9=True; C9=Asm4EE; D9=0; E9=0; F9=0; G9=0; H9=0; I9=0; A10(AssemblyScrew004)=Assembly.Screw004; B10=True; C10=Asm4EE; D10=0; E10=0; F10=0; G10=0; H10=0; I10=0; A11(AssemblyScrew003)=Assembly.Screw003; B11=True; C11=Asm4EE; D11=0; E11=0; F11=0; G11=0; H11=0; I11=0; A12(AssemblyScrew002)=Assembly.Screw002; B12=True; C12=Asm4EE; D12=0; E12=0; F12=0; G12=0; H12=0; I12=0; A13(AssemblyNut005)=Assembly.Nut005; B13=True; C13=Asm4EE; D13=0; E13=0; F13=-7.9; G13=0; H13=0; I13=180; A14(AssemblyNut002)=Assembly.Nut002; B14=True; C14=Asm4EE; D14=0; E14=0; F14=-7.9; G14=0; H14=0; I14=180; A15(AssemblyWasher003)=Assembly.Washer003; B15=True; C15=Asm4EE; D15=0; E15=0; F15=-7.2; G15=0; H15=0; I15=180; A16(AssemblyWasher)=Assembly.Washer; B16=True; C16=Asm4EE; D16=0; E16=0; F16=-7.2; G16=0; H16=0; I16=180; A17(AssemblyScrew014)=Assembly.Screw014; B17=True; C17=Asm4EE; D17=0; E17=0; F17=0; G17=0; H17=0; I17=0; A18(AssemblyScrew015)=Assembly.Screw015; B18=True; C18=Asm4EE; D18=0; E18=0; F18=0; G18=0; H18=0; I18=0; A19(AssemblyScrew010)=Assembly.Screw010; B19=True; C19=Asm4EE; D19=0; E19=0; F19=0; G19=0; H19=0; I19=0; A20(AssemblyScrew013)=Assembly.Screw013; B20=True; C20=Asm4EE; D20=0; E20=0; F20=0; G20=0; H20=0; I20=0; A21(AssemblyScrew012)=Assembly.Screw012; B21=True; C21=Asm4EE; D21=0; E21=0; F21=0; G21=0; H21=0; I21=0; A22(AssemblyScrew011)=Assembly.Screw011; B22=True; C22=Asm4EE; D22=0; E22=0; F22=0; G22=0; H22=0; I22=0; A23(AssemblyScrew009)=Assembly.Screw009; B23=True; C23=Asm4EE; D23=0; E23=0; F23=0; G23=0; H23=0; I23=0; A24(AssemblyScrew008)=Assembly.Screw008; B24=True; C24=Asm4EE; D24=0; E24=0; F24=0; G24=0; H24=0; I24=0; A25(AssemblyScrew007)=Assembly.Screw007; B25=True; C25=Asm4EE; D25=0; E25=0; F25=0; G25=0; H25=0; I25=0; +246 more cells
FEATURE [Spreadsheet::Sheet] Inside
  cells = A1=Asm4::ConfigurationTable; A2=0; A4=ObjectName; B4=Visible; C4=Assembly Type; D4=Pos. X; E4=Pos. Y; F4=Pos. Z; G4=Rot. Yaw; H4=Rot. Pitch; I4=Rot. Roll; A5(AssemblyFuse_Holder_01500274ZXU)=Assembly.Fuse_Holder_01500274ZXU; B5=True; C5=Asm4EE; D5=-52; E5=-10; F5=22; G5=0; H5=90; I5=180; A6(AssemblyNut004)=Assembly.Nut004; B6=True; C6=Asm4EE; D6=0; E6=0; F6=0.6; G6=0; H6=0; I6=0; A7(AssemblyWasher002)=Assembly.Washer002; B7=True; C7=Asm4EE; D7=0; E7=0; F7=0; G7=180; H7=2.291831180523293e-14; I7=2.291831180523293e-14; A8(AssemblyScrew016)=Assembly.Screw016; B8=True; C8=Asm4EE; D8=0; E8=0; F8=0; G8=0; H8=0; I8=0; A9(AssemblyScrew005)=Assembly.Screw005; B9=True; C9=Asm4EE; D9=0; E9=0; F9=0; G9=0; H9=0; I9=0; A10(AssemblyScrew004)=Assembly.Screw004; B10=True; C10=Asm4EE; D10=0; E10=0; F10=0; G10=0; H10=0; I10=0; A11(AssemblyScrew003)=Assembly.Screw003; B11=True; C11=Asm4EE; D11=0; E11=0; F11=0; G11=0; H11=0; I11=0; A12(AssemblyScrew002)=Assembly.Screw002; B12=True; C12=Asm4EE; D12=0; E12=0; F12=0; G12=0; H12=0; I12=0; A13(AssemblyNut005)=Assembly.Nut005; B13=True; C13=Asm4EE; D13=0; E13=0; F13=-7.9; G13=0; H13=0; I13=180; A14(AssemblyNut002)=Assembly.Nut002; B14=True; C14=Asm4EE; D14=0; E14=0; F14=-7.9; G14=0; H14=0; I14=180; A15(AssemblyWasher003)=Assembly.Washer003; B15=True; C15=Asm4EE; D15=0; E15=0; F15=-7.2; G15=0; H15=0; I15=180; A16(AssemblyWasher)=Assembly.Washer; B16=True; C16=Asm4EE; D16=0; E16=0; F16=-7.2; G16=0; H16=0; I16=180; A17(AssemblyScrew014)=Assembly.Screw014; B17=True; C17=Asm4EE; D17=0; E17=0; F17=0; G17=0; H17=0; I17=0; A18(AssemblyScrew015)=Assembly.Screw015; B18=True; C18=Asm4EE; D18=0; E18=0; F18=0; G18=0; H18=0; I18=0; A19(AssemblyScrew010)=Assembly.Screw010; B19=True; C19=Asm4EE; D19=0; E19=0; F19=0; G19=0; H19=0; I19=0; A20(AssemblyScrew013)=Assembly.Screw013; B20=True; C20=Asm4EE; D20=0; E20=0; F20=0; G20=0; H20=0; I20=0; A21(AssemblyScrew012)=Assembly.Screw012; B21=True; C21=Asm4EE; D21=0; E21=0; F21=0; G21=0; H21=0; I21=0; A22(AssemblyScrew011)=Assembly.Screw011; B22=True; C22=Asm4EE; D22=0; E22=0; F22=0; G22=0; H22=0; I22=0; A23(AssemblyScrew009)=Assembly.Screw009; B23=True; C23=Asm4EE; D23=0; E23=0; F23=0; G23=0; H23=0; I23=0; A24(AssemblyScrew008)=Assembly.Screw008; B24=True; C24=Asm4EE; D24=0; E24=0; F24=0; G24=0; H24=0; I24=0; A25(AssemblyScrew007)=Assembly.Screw007; B25=True; C25=Asm4EE; D25=0; E25=0; F25=0; G25=0; H25=0; I25=0; +246 more cells
FEATURE [Spreadsheet::Sheet] Exploded
  cells = A1=Asm4::ConfigurationTable; A2=0; A4=ObjectName; B4=Visible; C4=Assembly Type; D4=Pos. X; E4=Pos. Y; F4=Pos. Z; G4=Rot. Yaw; H4=Rot. Pitch; I4=Rot. Roll; A5(AssemblyFuse_Holder_01500274ZXU)=Assembly.Fuse_Holder_01500274ZXU; B5=True; C5=Asm4EE; D5=-30; E5=-40; F5=40; G5=0; H5=90; I5=180; A6(AssemblyNut004)=Assembly.Nut004; B6=True; C6=Asm4EE; D6=0; E6=0; F6=80; G6=180; H6=0; I6=0; A7(AssemblyWasher002)=Assembly.Washer002; B7=True; C7=Asm4EE; D7=0; E7=0; F7=70; G7=180; H7=0; I7=0; A8(AssemblyScrew016)=Assembly.Screw016; B8=True; C8=Asm4EE; D8=0; E8=0; F8=40; G8=0; H8=0; I8=0; A9(AssemblyScrew005)=Assembly.Screw005; B9=True; C9=Asm4EE; D9=0; E9=0; F9=20; G9=0; H9=0; I9=0; A10(AssemblyScrew004)=Assembly.Screw004; B10=True; C10=Asm4EE; D10=0; E10=0; F10=20; G10=0; H10=0; I10=0; A11(AssemblyScrew003)=Assembly.Screw003; B11=True; C11=Asm4EE; D11=0; E11=0; F11=20; G11=0; H11=0; I11=0; A12(AssemblyScrew002)=Assembly.Screw002; B12=True; C12=Asm4EE; D12=0; E12=0; F12=20; G12=0; H12=0; I12=0; A13(AssemblyNut005)=Assembly.Nut005; B13=True; C13=Asm4EE; D13=0; E13=0; F13=-70; G13=0; H13=0; I13=180; A14(AssemblyNut002)=Assembly.Nut002; B14=True; C14=Asm4EE; D14=0; E14=0; F14=-70; G14=0; H14=0; I14=180; A15(AssemblyWasher003)=Assembly.Washer003; B15=True; C15=Asm4EE; D15=0; E15=0; F15=-60; G15=0; H15=0; I15=180; A16(AssemblyWasher)=Assembly.Washer; B16=True; C16=Asm4EE; D16=0; E16=0; F16=-60; G16=0; H16=0; I16=180; A17(AssemblyScrew014)=Assembly.Screw014; B17=True; C17=Asm4EE; D17=0; E17=0; F17=25; G17=0; H17=0; I17=0; A18(AssemblyScrew015)=Assembly.Screw015; B18=True; C18=Asm4EE; D18=0; E18=0; F18=25; G18=0; H18=0; I18=0; A19(AssemblyScrew010)=Assembly.Screw010; B19=True; C19=Asm4EE; D19=0; E19=0; F19=60; G19=0; H19=0; I19=0; A20(AssemblyScrew013)=Assembly.Screw013; B20=True; C20=Asm4EE; D20=0; E20=0; F20=60; G20=0; H20=0; I20=0; A21(AssemblyScrew012)=Assembly.Screw012; B21=True; C21=Asm4EE; D21=0; E21=0; F21=60; G21=0; H21=0; I21=0; A22(AssemblyScrew011)=Assembly.Screw011; B22=True; C22=Asm4EE; D22=0; E22=0; F22=60; G22=0; H22=0; I22=0; A23(AssemblyScrew009)=Assembly.Screw009; B23=True; C23=Asm4EE; D23=0; E23=0; F23=50; G23=0; H23=0; I23=0; A24(AssemblyScrew008)=Assembly.Screw008; B24=True; C24=Asm4EE; D24=0; E24=0; F24=50; G24=0; H24=0; I24=0; A25(AssemblyScrew007)=Assembly.Screw007; B25=True; C25=Asm4EE; D25=0; E25=0; F25=50; G25=0; H25=0; I25=0; +246 more cells
FEATURE [App::DocumentObjectGroup] Configurations
  Group = -> [Default,Inside,Exploded]
FEATURE [Spreadsheet::Sheet] Spreadsheet  label="BOM"
  cells = A1=Position; B1=Component; C1=Part Number / Specification; D1=Manufacturer; E1=Material; F1=Qty; G1=Description; A2=1; B2=Enclosure; C2=1455Q1602BK; D2=Hammond; E2=-; F2=1; A3=2; B3=PCBA; C3=OpenSolder PCBA; D3=DIY; E3=-; F3=1; A4=3; B4=Front Panel; C4=OpenSolder Front Panel; D4=DIY; E4=ABS; F4=1; G4=Alternative material: Aluminium sheet; A5=4; B5=Rear Panel; C5=OpenSolder Front Panel; D5=DIY; E5=ABS; F5=1; G5=Alternative material: Aluminium sheet; A6=5; B6=Transformer Spacer; C6=OpenSolder Transformer Spacer; D6=DIY; E6=ABS; F6=1; A7=6; B7=Transformer kit; C7=TI-044229-ME-ES; D7=Noratel; E7=-; F7=1; G7=24VAC, 100VA min, D105xH46 max size; A8=7; B8=IDC Power Inlet; C8=703W-00/04; D8=Qualtek; E8=-; F8=1; A9=8; B9=Power Switch; C9=CWSB11AA2F; D9=NKK Switches; E9=-; F9=1; A10=9; B10=Fuse holder inline; C10=01500274ZXU; D10=Littelfuse Inc.; E10=-; F10=1; A11=10; B11=Connector; C11=MJ-064H; D11=Marushin Electric; E11=-; F11=2; A12=11; B12=Rubber Pads; C12=Self adhesive; D12=-; E12=-; F12=4; A13=12; B13=Knob; C13=Ø6, D-shaft, set screw; D13=-; E13=-; F13=1; A14=13; B14=Socket Head Cap Screw M3x8; C14=ISO 4762; D14=-; E14=-; F14=4; A15=14; B15=Socket Head Cap Screw M3x12; C15=ISO 4762; D15=-; E15=-; F15=2; A16=15; B16=CS Flat Head Screw M3X12; C16=ISO 10642; D16=-; E16=-; F16=1; A17=16; B17=Washer M3; C17=ISO 7089; D17=-; E17=-; F17=3; A18=17; B18=Locknut M3; C18=ISO 10511; D18=-; E18=-; F18=3; A19=18; B19=Button Head Screw M3.5x16; C19=ISO 7380; D19=-; E19=-; F19=8; A20=19; B20=CS Flat Head Screw M5x20; C20=ISO 10642; D20=-; E20=-; F20=2; A21=20; B21=Locknut M5; C21=ISO 10511; D21=-; E21=-; F21=2
FEATURE [App::Link] Fuse_Holder_01500274ZXU
  AssemblyType = Part::Link
  AttachedBy = #LCS_0
  AttachedTo = _455Q1602BK_Extrusion#LCS_Extrusion
  AttachmentOffset = pos=(-52,-10,22) rot=(0.707107,0,-0.707107;3.14159rad)
  LinkPlacement = pos=(-52,22,10) rot=(0.57735,-0.57735,-0.57735;2.0944rad)
  LinkedObject = -> <external Parts/Fuse Holder Inline.FCStd>#Fuse_Holder_01500274ZXU
  Placement = pos=(-52,22,10) rot=(0.57735,-0.57735,-0.57735;2.0944rad)
  SolverId = Asm4EE
  expr: Placement = _455Q1602BK_Extrusion.Placement * Enclosure_1455Q1602BK#LCS_Extrusion.Placement * AttachmentOffset * Fuse_Holder_Inline#LCS_0.Placement ^ -1
FEATURE [App::DocumentObjectGroup] Linked_Parts  label="Parts"
  Group = -> [_455Q1602BK_Extrusion,_455Q1602BK_Cap,Transformer_Spacer,Transformer_Group,Front_Panel,Rear_Panel,openSolderV0_2_PCBA,Connector_Holder,Connector_STlink,_03W_00_IEC_C14_Connector,CWSB11AA2F_Switch,Fuse_Holder_01500274ZXU,Knob,Rubber_Pads]
FEATURE [App::Part] Assembly
  AssemblyType = Part::Link
  Group = -> [LCS_Origin,Variables,Constraints,Configurations,LCS,Linked_Parts,Fasteners,_455Q1602BK_Extrusion,_455Q1602BK_Cap,Transformer_Spacer,Screw,Transformer_Fasteners,Panel_Fasteners,Nut,Nut001,Transformer_Group,Foam_Bottom,Transformer,Foam_Top,Transformer_Washer,Screw001,Front_Panel_Sketch,Front_Panel_Sketch001,LCS_Assembly_Front_Hole,LCS_Assembly_Rear_Hole,Front_Panel,Rear_Panel,openSolderV0_2_PCBA,+43 more]
  Origin = -> Origin
  Type = Assembly
FEATURE [TechDraw::DrawSVGTemplate] Template
  EditableTexts = AUTHOR_NAME=Håvard Jakobsen; DN=-; DRAWING_TITLE=OpenSolder Station Assembly Drawing; FC-DATE=20220501; FC-REV=REV 1; FC-SC=7/10; FC-SH=1/3; FC-SI=A3; PN=-; SI-1=Assembled station overview; SI-5=https://github.com/<owner>/OpenSolder; SI-6=Licence: GPL-3.0
  Height = 297
  Orientation = 1
  Width = 420
FEATURE [TechDraw::DrawProjGroupItem] ProjItem  label="Front"
  CoarseView = false
  Direction = (1,0,0)
  Focus = 100
  HardHidden = false
  IsoCount = 0
  IsoHidden = false
  IsoVisible = false
  LockPosition = true
  Perspective = false
  Rotation = 0
  RotationVector = (0,1,0)
  Scale = 0.7
  ScaleType = 2
  SeamHidden = false
  SeamVisible = true
  SmoothHidden = false
  SmoothVisible = true
  Source = -> [Assembly]
  Type = 0
  X = 0
  XDirection = (0,1,0)
  Y = 0
FEATURE [TechDraw::DrawProjGroupItem] ProjItem001  label="Right"
  CoarseView = false
  Direction = (1e-16,1,0)
  Focus = 100
  HardHidden = false
  IsoCount = 0
  IsoHidden = false
  IsoVisible = false
  LockPosition = false
  Perspective = false
  Rotation = 0
  RotationVector = (1,0,0)
  Scale = 0.7
  ScaleType = 2
  SeamHidden = false
  SeamVisible = true
  SmoothHidden = false
  SmoothVisible = true
  Source = -> [Assembly]
  Type = 2
  X = -125.305
  XDirection = (-1,1e-16,0)
  Y = 0
FEATURE [TechDraw::DrawProjGroupItem] ProjItem002  label="Left"
  CoarseView = false
  Direction = (1e-16,-1,0)
  Focus = 100
  HardHidden = false
  IsoCount = 0
  IsoHidden = false
  IsoVisible = false
  LockPosition = false
  Perspective = false
  Rotation = 0
  RotationVector = (1,0,0)
  ScaleType = 2
  SeamHidden = false
  SeamVisible = true
  SmoothHidden = false
  SmoothVisible = true
  Source = -> [Assembly]
  Type = 1
  X = 125.335
  XDirection = (1,1e-16,0)
  Y = 0
FEATURE [TechDraw::DrawProjGroup] ProjGroup
  Anchor = -> ProjItem
  AutoDistribute = true
  LockPosition = false
  ProjectionType = 0
  Rotation = 0
  Scale = 0.7
  ScaleType = 0
  Source = -> [Assembly]
  Views = -> [ProjItem,ProjItem001,ProjItem002]
  X = 214.243
  Y = 228.116
  spacingX = 15
  spacingY = 15
FEATURE [TechDraw::DrawViewPart] View
  CoarseView = false
  Direction = (0.577,-0.577,0.577)
  Focus = 100
  HardHidden = false
  IsoCount = 0
  IsoHidden = false
  IsoVisible = false
  LockPosition = false
  Perspective = false
  Rotation = 0
  ScaleType = 0
  SeamHidden = false
  SeamVisible = true
  SmoothHidden = false
  SmoothVisible = true
  Source = -> [Assembly]
  X = 125.277
  XDirection = (0.707,0.707,0)
  Y = 100
FEATURE [TechDraw::DrawViewDimension] Dimension001
  AngleOverride = false
  Arbitrary = false
  ArbitraryTolerances = false
  EqualTolerance = true
  ExtensionAngle = 0
  FormatSpec = %.2f
  FormatSpecOverTolerance = %+.2f
  FormatSpecUnderTolerance = %+.2f
  Inverted = false
  LineAngle = 0
  LockPosition = false
  MeasureType = 1
  OverTolerance = 0
  References2D = -> [ProjItem002]
  Rotation = 0
  ScaleType = 1
  TheoreticalExact = false
  Type = 1
  UnderTolerance = 0
  X = 0
  Y = -25
FEATURE [TechDraw::DrawViewDimension] Dimension002
  AngleOverride = false
  Arbitrary = false
  ArbitraryTolerances = false
  EqualTolerance = true
  ExtensionAngle = 0
  FormatSpec = %.2f
  FormatSpecOverTolerance = %+.2f
  FormatSpecUnderTolerance = %+.2f
  Inverted = false
  LineAngle = 0
  LockPosition = false
  MeasureType = 1
  OverTolerance = 0
  References2D = -> [ProjItem]
  Rotation = 0
  ScaleType = 1
  TheoreticalExact = false
  Type = 1
  UnderTolerance = 0
  X = 0
  Y = -25
FEATURE [TechDraw::DrawViewBalloon] Balloon001
  BubbleShape = 6
  EndType = 0
  EndTypeScale = 1
  KinkLength = 5
  LockPosition = false
  OriginX = -47.5
  OriginY = 21.1554
  Rotation = 0
  ScaleType = 2
  ShapeScale = 1
  SourceView = -> ProjItem001
  Text = ST-link interface connector
  TextWrapLen = -1
  X = 20
  Y = 60
FEATURE [TechDraw::DrawViewBalloon] Balloon
  BubbleShape = 6
  EndType = 0
  EndTypeScale = 1
  KinkLength = 5
  LockPosition = false
  OriginX = -47.5
  OriginY = -18.6446
  Rotation = 0
  ScaleType = 2
  ShapeScale = 1
  SourceView = -> ProjItem001
  Text = Handpiece stand connector
  TextWrapLen = -1
  X = 20
  Y = -60
FEATURE [TechDraw::DrawViewDimension] Dimension
  AngleOverride = false
  Arbitrary = false
  ArbitraryTolerances = false
  EqualTolerance = true
  ExtensionAngle = 0
  FormatSpec = %.2f
  FormatSpecOverTolerance = %+.2f
  FormatSpecUnderTolerance = %+.2f
  Inverted = false
  LineAngle = 0
  LockPosition = false
  MeasureType = 1
  OverTolerance = 0
  References2D = -> [ProjItem002]
  Rotation = 0
  ScaleType = 1
  TheoreticalExact = false
  Type = 2
  UnderTolerance = 0
  X = 55
  Y = 2
FEATURE [TechDraw::DrawPage] Page  label="Page_1"
  KeepUpdated = false
  NextBalloonIndex = 4
  ProjectionType = 0
  Scale = 0.7
  Template = -> Template
  Views = -> [ProjGroup,View,Dimension001,Dimension002,Balloon001,Balloon,Dimension]
FEATURE [TechDraw::DrawSVGTemplate] Template001
  EditableTexts = AUTHOR_NAME=Håvard Jakobsen; DN=-; DRAWING_TITLE=OpenSolder Station Assembly Drawing; FC-DATE=20220501; FC-REV=REV 1; FC-SC=3:4; FC-SH=2/3; FC-SI=A3; PN=-; SI-1=Exploded view; SI-5=https://github.com/<owner>/OpenSolder; SI-6=Licence: GPL-3.0
  Height = 297
  Orientation = 1
  Width = 420
FEATURE [TechDraw::DrawViewPart] View001
  CoarseView = false
  Direction = (0.809,-0.27,0.523)
  Focus = 100
  HardHidden = false
  IsoCount = 0
  IsoHidden = false
  IsoVisible = false
  LockPosition = true
  Perspective = false
  Rotation = 0
  Scale = 0.75
  ScaleType = 0
  SeamHidden = false
  SeamVisible = true
  SmoothHidden = false
  SmoothVisible = true
  Source = -> [Assembly]
  X = 215
  XDirection = (0.317,0.949,0)
  Y = 180
FEATURE [TechDraw::DrawSVGTemplate] Template002
  EditableTexts = AUTHOR_NAME=Håvard Jakobsen; DN=-; DRAWING_TITLE=OpenSolder Station Assembly Drawing; FC-DATE=20220501; FC-REV=REV 1; FC-SC=1:1; FC-SH=3/3; FC-SI=A3; PN=-; SI-1=Bill of Materials; SI-5=https://github.com/<owner>/OpenSolder; SI-6=Licence: GPL-3.0
  Height = 297
  Orientation = 1
  Width = 420
FEATURE [TechDraw::DrawViewSpreadsheet] Sheet
  CellEnd = G21
  CellStart = A1
  Font = osifont
  LineWidth = 1
  LockPosition = true
  Rotation = 0
  Scale = 1.2
  ScaleType = 2
  Source = -> Spreadsheet
  Symbol = <blob: 29784 chars omitted>
  TextSize = 12
  X = 215
  Y = 180
FEATURE [TechDraw::DrawPage] Page002  label="Page_3"
  KeepUpdated = false
  NextBalloonIndex = 1
  ProjectionType = 0
  Template = -> Template002
  Views = -> [Sheet]
FEATURE [TechDraw::DrawViewBalloon] Balloon002
  BubbleShape = 0
  EndType = 0
  EndTypeScale = 1
  KinkLength = 5
  LockPosition = false
  OriginX = 63.2095
  OriginY = -80.16
  Rotation = 0
  ScaleType = 1
  ShapeScale = 1
  SourceView = -> View001
  Text = 1
  TextWrapLen = -1
  X = 99.1364
  Y = -115.789
FEATURE [TechDraw::DrawViewBalloon] Balloon003
  BubbleShape = 0
  EndType = 0
  EndTypeScale = 1
  KinkLength = 5
  LockPosition = false
  OriginX = -38.449
  OriginY = -87.8248
  Rotation = 0
  ScaleType = 1
  ShapeScale = 1
  SourceView = -> View001
  Text = 2
  TextWrapLen = -1
  X = -59.9915
  Y = -133.275
FEATURE [TechDraw::DrawViewBalloon] Balloon004
  BubbleShape = 0
  EndType = 0
  EndTypeScale = 1
  KinkLength = 5
  LockPosition = false
  OriginX = -73.5255
  OriginY = -103.647
  Rotation = 0
  ScaleType = 1
  ShapeScale = 1
  SourceView = -> View001
  Text = 3
  TextWrapLen = -1
  X = -103.262
  Y = -140.399
FEATURE [TechDraw::DrawViewBalloon] Balloon005
  BubbleShape = 0
  EndType = 0
  EndTypeScale = 1
  KinkLength = 5
  LockPosition = false
  OriginX = 161.713
  OriginY = -62.5718
  Rotation = 0
  ScaleType = 1
  ShapeScale = 1
  SourceView = -> View001
  Text = 4
  TextWrapLen = -1
  X = 204.936
  Y = -94.5531
FEATURE [TechDraw::DrawViewBalloon] Balloon006
  BubbleShape = 0
  EndType = 0
  EndTypeScale = 1
  KinkLength = 5
  LockPosition = false
  OriginX = 33.9176
  OriginY = -15.2011
  Rotation = 0
  ScaleType = 1
  ShapeScale = 1
  SourceView = -> View001
  Text = 5
  TextWrapLen = -1
  X = -23.2626
  Y = 26.2819
FEATURE [TechDraw::DrawViewBalloon] Balloon007
  BubbleShape = 0
  EndType = 0
  EndTypeScale = 1
  KinkLength = 5
  LockPosition = false
  OriginX = -6.93561
  OriginY = 70.9259
  Rotation = 0
  ScaleType = 1
  ShapeScale = 1
  SourceView = -> View001
  Text = 6
  TextWrapLen = -1
  X = -37.1771
  Y = 84.7966
FEATURE [TechDraw::DrawViewBalloon] Balloon008
  BubbleShape = 0
  EndType = 0
  EndTypeScale = 1
  KinkLength = 5
  LockPosition = false
  OriginX = 180.074
  OriginY = -4.4412
  Rotation = 0
  ScaleType = 1
  ShapeScale = 1
  SourceView = -> View001
  Text = 7
  TextWrapLen = -1
  X = 234.67
  Y = 24.3602
FEATURE [TechDraw::DrawViewBalloon] Balloon009
  BubbleShape = 0
  EndType = 0
  EndTypeScale = 1
  KinkLength = 5
  LockPosition = false
  OriginX = 173.414
  OriginY = 26.9012
  Rotation = 0
  ScaleType = 1
  ShapeScale = 1
  SourceView = -> View001
  Text = 8
  TextWrapLen = -1
  X = 226.053
  Y = 50.1879
FEATURE [TechDraw::DrawViewBalloon] Balloon010
  BubbleShape = 0
  EndType = 0
  EndTypeScale = 1
  KinkLength = 5
  LockPosition = false
  OriginX = 88.4864
  OriginY = 10.8845
  Rotation = 0
  ScaleType = 1
  ShapeScale = 1
  SourceView = -> View001
  Text = 9
  TextWrapLen = -1
  X = 144.683
  Y = 80.4228
FEATURE [TechDraw::DrawViewBalloon] Balloon011
  BubbleShape = 0
  EndType = 0
  EndTypeScale = 1
  KinkLength = 5
  LockPosition = false
  OriginX = 196.679
  OriginY = -19.6903
  Rotation = 0
  ScaleType = 1
  ShapeScale = 1
  SourceView = -> View001
  Text = 10
  TextWrapLen = -1
  X = 235.442
  Y = -30.0249
FEATURE [TechDraw::DrawViewBalloon] Balloon012
  BubbleShape = 0
  EndType = 0
  EndTypeScale = 1
  KinkLength = 5
  LockPosition = false
  OriginX = 6.08555
  OriginY = -120.703
  Rotation = 0
  ScaleType = 1
  ShapeScale = 1
  SourceView = -> View001
  Text = 11
  TextWrapLen = -1
  X = 36.026
  Y = -128.178
FEATURE [TechDraw::DrawViewBalloon] Balloon013
  BubbleShape = 0
  EndType = 0
  EndTypeScale = 1
  KinkLength = 5
  LockPosition = false
  OriginX = -108.7
  OriginY = -84.2002
  Rotation = 0
  ScaleType = 1
  ShapeScale = 1
  SourceView = -> View001
  Text = 12
  TextWrapLen = -1
  X = -152.309
  Y = -95.5627
FEATURE [TechDraw::DrawViewBalloon] Balloon014
  BubbleShape = 0
  EndType = 0
  EndTypeScale = 1
  KinkLength = 5
  LockPosition = false
  OriginX = -129.689
  OriginY = -26.4788
  Rotation = 0
  ScaleType = 1
  ShapeScale = 1
  SourceView = -> View001
  Text = 13
  TextWrapLen = -1
  X = -174.186
  Y = -32.5872
FEATURE [TechDraw::DrawViewBalloon] Balloon015
  BubbleShape = 0
  EndType = 0
  EndTypeScale = 1
  KinkLength = 5
  LockPosition = false
  OriginX = 206.646
  OriginY = -0.806087
  Rotation = 0
  ScaleType = 1
  ShapeScale = 1
  SourceView = -> View001
  Text = 14
  TextWrapLen = -1
  X = 236.693
  Y = 2.55688
FEATURE [TechDraw::DrawViewBalloon] Balloon016
  BubbleShape = 0
  EndType = 0
  EndTypeScale = 1
  KinkLength = 5
  LockPosition = false
  OriginX = 113.49
  OriginY = -77.9338
  Rotation = 0
  ScaleType = 1
  ShapeScale = 1
  SourceView = -> View001
  Text = 15
  TextWrapLen = -1
  X = 154.388
  Y = -84.5327
FEATURE [TechDraw::DrawViewBalloon] Balloon017
  BubbleShape = 0
  EndType = 0
  EndTypeScale = 1
  KinkLength = 5
  LockPosition = false
  OriginX = 115.478
  OriginY = 11.6045
  Rotation = 0
  ScaleType = 1
  ShapeScale = 1
  SourceView = -> View001
  Text = 16
  TextWrapLen = -1
  X = 152.64
  Y = 40.4059
FEATURE [TechDraw::DrawViewBalloon] Balloon018
  BubbleShape = 0
  EndType = 0
  EndTypeScale = 1
  KinkLength = 5
  LockPosition = false
  OriginX = 113.8
  OriginY = 23.251
  Rotation = 0
  ScaleType = 1
  ShapeScale = 1
  SourceView = -> View001
  Text = 17
  TextWrapLen = -1
  X = 152.919
  Y = 61.8364
FEATURE [TechDraw::DrawViewBalloon] Balloon019
  BubbleShape = 0
  EndType = 0
  EndTypeScale = 1
  KinkLength = 5
  LockPosition = false
  OriginX = -121.76
  OriginY = -110.71
  Rotation = 0
  ScaleType = 1
  ShapeScale = 1
  SourceView = -> View001
  Text = 18
  TextWrapLen = -1
  X = -160.4
  Y = -128.305
FEATURE [TechDraw::DrawViewBalloon] Balloon020
  BubbleShape = 0
  EndType = 0
  EndTypeScale = 1
  KinkLength = 5
  LockPosition = false
  OriginX = 40.1576
  OriginY = 120.717
  Rotation = 0
  ScaleType = 1
  ShapeScale = 1
  SourceView = -> View001
  Text = 19
  TextWrapLen = -1
  X = -8.94105
  Y = 128.19
FEATURE [TechDraw::DrawViewBalloon] Balloon021
  BubbleShape = 0
  EndType = 0
  EndTypeScale = 1
  KinkLength = 5
  LockPosition = false
  OriginX = 14.4672
  OriginY = -21.2752
  Rotation = 0
  ScaleType = 1
  ShapeScale = 1
  SourceView = -> View001
  Text = 20
  TextWrapLen = -1
  X = -19.5767
  Y = -6.39204
FEATURE [TechDraw::DrawPage] Page001  label="Page_2"
  KeepUpdated = false
  NextBalloonIndex = 21
  ProjectionType = 0
  Scale = 0.75
  Template = -> Template001
  Views = -> [View001,Balloon002,Balloon003,Balloon004,Balloon005,Balloon006,Balloon007,Balloon008,Balloon009,Balloon010,Balloon011,Balloon012,Balloon013,Balloon014,Balloon015,Balloon016,Balloon017,Balloon018,Balloon019,Balloon020,Balloon021]
FEATURE [TechDraw::DrawSVGTemplate] Template003
  EditableTexts = AUTHOR_NAME=Håvard Jakobsen; DN=-; DRAWING_TITLE=Enclosure Drawing; FC-DATE=20220501; FC-REV=REV 1; FC-SC=7/10; FC-SH=1/1; FC-SI=A3; PN=-; SI-1=Modify enclosure Hammond 1455Q1602BK; SI-2=according to drawing; SI-5=https://github.com/<owner>/OpenSolder; SI-6=Licence: GPL-3.0
  Height = 297
  Orientation = 1
  Width = 420
FEATURE [TechDraw::DrawProjGroupItem] ProjItem003  label="Front001"
  CoarseView = false
  Direction = (0,-1,0)
  Focus = 100
  HardHidden = false
  IsoCount = 0
  IsoHidden = false
  IsoVisible = false
  LockPosition = true
  Perspective = false
  Rotation = 0
  RotationVector = (1,0,0)
  Scale = 0.7
  ScaleType = 2
  SeamHidden = false
  SeamVisible = true
  SmoothHidden = false
  SmoothVisible = true
  Type = 0
  X = 0
  XDirection = (1,0,0)
  XSource = -> [_455Q1602BK_Extrusion]
  Y = 0
FEATURE [TechDraw::DrawProjGroupItem] ProjItem005  label="FrontTopRight"
  CoarseView = false
  Direction = (0.57735,-0.57735,0.57735)
  Focus = 100
  HardHidden = false
  IsoCount = 0
  IsoHidden = false
  IsoVisible = false
  LockPosition = true
  Perspective = false
  Rotation = 0
  RotationVector = (1,0,0)
  Scale = 0.7
  ScaleType = 2
  SeamHidden = false
  SeamVisible = true
  SmoothHidden = false
  SmoothVisible = true
  Type = 7
  X = 200
  XDirection = (0.707107,0.707107,0)
  XSource = -> [_455Q1602BK_Extrusion]
  Y = 0
FEATURE [TechDraw::DrawProjGroup] ProjGroup001
  Anchor = -> ProjItem003
  AutoDistribute = true
  LockPosition = true
  ProjectionType = 0
  Rotation = 0
  Scale = 0.7
  ScaleType = 0
  Views = -> [ProjItem003,ProjItem005]
  X = 120
  XSource = -> [_455Q1602BK_Extrusion]
  Y = 200
  spacingX = 15
  spacingY = 15
FEATURE [TechDraw::DrawViewSection] SectionView  label="Section A - A"
  BaseView = -> ProjItem003
  Caption = A - A
  CoarseView = false
  CutSurfaceDisplay = 2
  Direction = (0,0,1)
  FileGeomPattern = <path>
  FileHatchPattern = <path>
  Focus = 100
  FuseBeforeCut = false
  HardHidden = false
  HatchScale = 1
  IsoCount = 0
  IsoHidden = false
  IsoVisible = false
  LockPosition = true
  NameGeomPattern = Diamond
  Perspective = false
  Rotation = 0
  Scale = 0.7
  ScaleType = 0
  SeamHidden = false
  SeamVisible = true
  SectionDirection = 3
  SectionNormal = (0,0,1)
  SectionOrigin = (0,25.75,0)
  SectionSymbol = A
  SmoothHidden = false
  SmoothVisible = true
  X = 120
  XDirection = (1,0,0)
  Y = 80
FEATURE [TechDraw::DrawViewDimension] Dimension003
  AngleOverride = false
  Arbitrary = false
  ArbitraryTolerances = false
  EqualTolerance = true
  ExtensionAngle = 0
  FormatSpec = (%.2f)
  FormatSpecOverTolerance = %+.2f
  FormatSpecUnderTolerance = %+.2f
  Inverted = false
  LineAngle = 0
  LockPosition = false
  MeasureType = 1
  OverTolerance = 0
  References2D = -> [ProjItem003]
  Rotation = 0
  ScaleType = 1
  TheoreticalExact = false
  Type = 2
  UnderTolerance = 0
  X = -67.5
  Y = 0
FEATURE [TechDraw::DrawViewDimension] Dimension004
  AngleOverride = false
  Arbitrary = false
  ArbitraryTolerances = false
  EqualTolerance = true
  ExtensionAngle = 0
  FormatSpec = (%.2f)
  FormatSpecOverTolerance = %+.2f
  FormatSpecUnderTolerance = %+.2f
  Inverted = false
  LineAngle = 0
  LockPosition = false
  MeasureType = 1
  OverTolerance = 0
  References2D = -> [ProjItem003]
  Rotation = 0
  ScaleType = 1
  TheoreticalExact = false
  Type = 1
  UnderTolerance = 0
  X = 0
  Y = 75
FEATURE [TechDraw::DrawViewDimension] Dimension005
  AngleOverride = false
  Arbitrary = false
  ArbitraryTolerances = false
  EqualTolerance = true
  ExtensionAngle = 0
  FormatSpec = %.2f
  FormatSpecOverTolerance = %+.2f
  FormatSpecUnderTolerance = %+.2f
  Inverted = false
  LineAngle = 0
  LockPosition = false
  MeasureType = 1
  OverTolerance = 0
  References2D = -> [ProjItem003]
  Rotation = 0
  ScaleType = 1
  TheoreticalExact = false
  Type = 1
  UnderTolerance = 0
  X = 25
  Y = -70
FEATURE [TechDraw::DrawViewDimension] Dimension006
  AngleOverride = false
  Arbitrary = false
  ArbitraryTolerances = false
  EqualTolerance = true
  ExtensionAngle = 0
  FormatSpec = %.2f
  FormatSpecOverTolerance = %+.2f
  FormatSpecUnderTolerance = %+.2f
  Inverted = false
  LineAngle = 0
  LockPosition = false
  MeasureType = 1
  OverTolerance = 0
  References2D = -> [ProjItem003]
  Rotation = 0
  ScaleType = 1
  TheoreticalExact = false
  Type = 1
  UnderTolerance = 0
  X = 29
  Y = -60
FEATURE [TechDraw::DrawViewDimension] Dimension007
  AngleOverride = false
  Arbitrary = false
  ArbitraryTolerances = false
  EqualTolerance = true
  ExtensionAngle = 0
  FormatSpec = %.2f
  FormatSpecOverTolerance = %+.2f
  FormatSpecUnderTolerance = %+.2f
  Inverted = false
  LineAngle = 0
  LockPosition = false
  MeasureType = 1
  OverTolerance = 0
  References2D = -> [ProjItem003]
  Rotation = 0
  ScaleType = 1
  TheoreticalExact = false
  Type = 2
  UnderTolerance = 0
  X = 50
  Y = -25
FEATURE [TechDraw::DrawViewDimension] Dimension008
  AngleOverride = false
  Arbitrary = false
  ArbitraryTolerances = false
  EqualTolerance = true
  ExtensionAngle = 0
  FormatSpec = %.2f
  FormatSpecOverTolerance = %+.2f
  FormatSpecUnderTolerance = %+.2f
  Inverted = false
  LineAngle = 0
  LockPosition = false
  MeasureType = 1
  OverTolerance = 0
  References2D = -> [ProjItem003]
  Rotation = 0
  ScaleType = 1
  TheoreticalExact = false
  Type = 2
  UnderTolerance = 0
  X = 60
  Y = -25
FEATURE [TechDraw::DrawViewBalloon] Balloon022
  BubbleShape = 7
  EndType = 0
  EndTypeScale = 1
  KinkLength = 5
  LockPosition = false
  OriginX = 9
  OriginY = 5
  Rotation = 0
  ScaleType = 1
  ShapeScale = 1
  SourceView = -> ProjItem003
  Text = Ø8 THRU ⌵ 12.2 x 45°
  TextWrapLen = -1
  X = 125.369
  Y = 57.3189
FEATURE [TechDraw::DrawViewBalloon] Balloon023
  BubbleShape = 7
  EndType = 0
  EndTypeScale = 1
  KinkLength = 5
  LockPosition = false
  OriginX = 18
  OriginY = -68
  Rotation = 0
  ScaleType = 1
  ShapeScale = 1
  SourceView = -> ProjItem003
  Text = Ø3.4 THRU ⌵ 6.7 x 45°
  TextWrapLen = -1
  X = -80.5392
  Y = -100.546
FEATURE [TechDraw::DrawPage] Page003  label="Enclosure"
  KeepUpdated = false
  NextBalloonIndex = 3
  ProjectionType = 0
  Scale = 0.7
  Template = -> Template003
  Views = -> [ProjGroup001,SectionView,Dimension003,Dimension004,Dimension005,Dimension006,Dimension007,Dimension008,Balloon022,Balloon023]
  expr: Scale = 0.7
FEATURE [App::DocumentObjectGroup] Drawings
  Group = -> [Page,Page001,Page002,Page003]
note: 2 file-system paths scrubbed to <path> (originals preserved in the JSON sidecar)

RESOLVED EXTERNAL PARTS (link-assembly join: the EXTERNAL_REF files above that resolve inside this repo's crawl, each included once):
---- part Parts/PCB.FCStd = doc fcstd_6117a7fea47c ----
FCSTD DOCUMENT  (FreeCAD 0.20R28730 (Git))
Label: PCB
License: All rights reserved
LicenseURL: http://en.wikipedia.org/wiki/All_rights_reserved
objects: Part::Feature×7, App::Part×6, Sketcher::SketchObject×4, PartDesign::Pad×3, PartDesign::CoordinateSystem×1, PartDesign::Body×1
note: 19 computed .brp shape members not serialized (recipe doc carries the construction recipe); baked Part::Feature solids carry a one-line shape summary decoded from their .brp

FEATURE [Part::Feature] Part__Feature  label="COMPOUND"
  shape: bbox 11.5 x 6 x 9.6 mm, 10 faces (baked)
FEATURE [Part::Feature] Part__Feature001  label="COMPOUND001"
  shape: bbox 9 x 1.5 x 6 mm, 14 faces (baked)
FEATURE [App::Part] COMPOUND  label="COMPOUND002"
  Group = -> [Part__Feature,Part__Feature001]
  Origin = -> Origin
FEATURE [App::Part] PDSE1_DCDC
  Group = -> [COMPOUND]
  Origin = -> Origin001
  Placement = pos=(3.3075,7.8425,1.65) rot=(0,0,1;3.14159rad)
FEATURE [Part::Feature] Part__Feature002  label="COMPOUND003"
  shape: bbox 43 x 1.2 x 38.37 mm, 23 faces (baked)
FEATURE [Part::Feature] Part__Feature003  label="COMPOUND004"
  shape: bbox 42.4 x 1.8 x 27.5 mm, 11 faces (baked)
FEATURE [Part::Feature] Part__Feature004  label="COMPOUND005"
  shape: bbox 17.78 x 14 x 2.54 mm, 172 faces (baked)
FEATURE [App::Part] COMPOUND001  label="COMPOUND006"
  Group = -> [Part__Feature002,Part__Feature003,Part__Feature004]
  Origin = -> Origin002
FEATURE [App::Part] OLED_SSD1306_1_54
  Group = -> [COMPOUND001]
  Origin = -> Origin003
  Placement = pos=(0,5e-16,-3.95) rot=(0,0.707107,0.707107;3.14159rad)
FEATURE [Part::Feature] Part__Feature005  label="SOLID"
  shape: bbox 20.2 x 20.2 x 22.2 mm, 111 faces (baked)
FEATURE [App::Part] RPC1_12RB_6P  label="RPC1-12RB-6P"
  Group = -> [Part__Feature005]
  Origin = -> Origin004
  Placement = pos=(40,8e-16,-6.3) rot=(0,0,1;0rad)
FEATURE [Part::Feature] Part__Feature007  label="openSolderV0.2 PCB"
  shape: bbox 100 x 44 x 1.6 mm, 68 faces (baked)
FEATURE [Sketcher::SketchObject] Sketch
  AttachmentOffset = pos=(0,0,-7) rot=(0,0,1;0rad)
  FullyConstrained = true
  MapMode = 5
  Placement = pos=(0,0,-7) rot=(0,0,1;0rad)
  Support = -> [XY_Plane006]
  sketch-geometry (3):
    g0: Circle CenterX=-40 CenterY=0 CenterZ=0 NormalX=0 NormalY=0 NormalZ=1 AngleXU=0 Radius=5
    g1: Circle CenterX=40 CenterY=0 CenterZ=0 NormalX=0 NormalY=0 NormalZ=1 AngleXU=0 Radius=5
    g2: Circle CenterX=40 CenterY=0 CenterZ=0 NormalX=0 NormalY=0 NormalZ=1 AngleXU=0 Radius=10
  constraints (7):
    c: PointOnObject(g1,g-1)
    c: Coincident(g2,g1)
    c: Symmetric(g0,g1,g-2)
    c: DistanceX(g0,g1) = 80
    c: Equal(g1,g0)
    c: Diameter(g1) = 10
    c: Diameter(g2) = 20
FEATURE [PartDesign::CoordinateSystem] LCS_PCBA
  AttacherType = Attacher::AttachEngine3D
  MapMode = 11
  Placement = pos=(-40,0,-7) rot=(0,0,1;1.5708rad)
  Support = -> [Sketch]
FEATURE [Sketcher::SketchObject] Sketch001
  FullyConstrained = true
  MapMode = 5
  Placement = pos=(0,0,0) rot=(1,0,0;1.5708rad)
  Support = -> [XZ_Plane007]
  sketch-geometry (5):
    g0: LineSegment StartX=-6.25 StartY=-6.75 StartZ=0 EndX=-6.25 EndY=6.75 EndZ=0
    g1: LineSegment StartX=-6.25 StartY=6.75 StartZ=0 EndX=6.25 EndY=6.75 EndZ=0
    g2: LineSegment StartX=6.25 StartY=6.75 StartZ=0 EndX=6.25 EndY=-6.75 EndZ=0
    g3: LineSegment StartX=6.25 StartY=-6.75 StartZ=0 EndX=-6.25 EndY=-6.75 EndZ=0
    g4: GeomPoint X=0 Y=0 Z=0
  constraints (12):
    c: Coincident(g0,g1)
    c: Coincident(g1,g2)
    c: Coincident(g2,g3)
    c: Coincident(g3,g0)
    c: Horizontal(g1)
    c: Horizontal(g3)
    c: Vertical(g0)
    c: Vertical(g2)
    c: Symmetric(g1,g0,g4)
    c: Coincident(g4,g-1)
    c: DistanceY(g2,g2) = 13.5
    c: DistanceX(g1,g1) = 12.5
FEATURE [PartDesign::Pad] Pad
  Direction = (0,-1,2e-16)
  Length = 6.5
  Length2 = 10
  Placement = pos=(0,0,0) rot=(1,0,0;1.5708rad)
  Profile = -> Sketch001
  ReferenceAxis = -> Sketch001 [N_Axis]
  Refine = true
  Type = 0
FEATURE [Sketcher::SketchObject] Sketch002
  FullyConstrained = true
  MapMode = 5
  Placement = pos=(0,0,0) rot=(1,0,0;1.5708rad)
  Support = -> [XZ_Plane007]
  sketch-geometry (1):
    g0: Circle CenterX=0 CenterY=0 CenterZ=0 NormalX=0 NormalY=0 NormalZ=1 AngleXU=0 Radius=3.5
  constraints (2):
    c: Coincident(g0,g-1)
    c: Diameter(g0) = 7
FEATURE [PartDesign::Pad] Pad001
  BaseFeature = -> Pad
  Direction = (0,-1,2e-16)
  Length = 14
  Length2 = 10
  Placement = pos=(0,0,0) rot=(1,0,0;1.5708rad)
  Profile = -> Sketch002
  ReferenceAxis = -> Sketch002 [N_Axis]
  Refine = true
  Type = 0
FEATURE [Sketcher::SketchObject] Sketch003
  FullyConstrained = true
  MapMode = 5
  Placement = pos=(0,0,0) rot=(1,0,0;1.5708rad)
  Support = -> [XZ_Plane007]
  sketch-geometry (1):
    g0: Circle CenterX=0 CenterY=0 CenterZ=0 NormalX=0 NormalY=0 NormalZ=1 AngleXU=0 Radius=3
  constraints (2):
    c: Coincident(g0,g-1)
    c: Diameter(g0) = 6
FEATURE [PartDesign::Pad] Pad002
  BaseFeature = -> Pad001
  Direction = (0,-1,2e-16)
  Length = 25
  Length2 = 10
  Placement = pos=(0,0,0) rot=(1,0,0;1.5708rad)
  Profile = -> Sketch003
  ReferenceAxis = -> Sketch003 [N_Axis]
  Refine = true
  Type = 0
FEATURE [PartDesign::Body] Body  label="PEC11R"
  Group = -> [Sketch001,Pad,Sketch002,Pad001,Sketch003,Pad002]
  Origin = -> Origin007
  Placement = pos=(-40,0,0) rot=(1,0,0;1.5708rad)
  Tip = -> Pad002
FEATURE [App::Part] openSolderV0_2_1  label="openSolderV0.2_PCBA"
  Group = -> [PDSE1_DCDC,OLED_SSD1306_1_54,RPC1_12RB_6P,Part__Feature007,Body,Sketch,LCS_PCBA]
  Origin = -> Origin006
  Placement = pos=(0,0,0) rot=(0,0.707107,0.707107;3.14159rad)
---- part Parts/Panels.FCStd = doc fcstd_6d33e910ff6e ----
FCSTD DOCUMENT  (FreeCAD 0.20R28730 (Git))
Label: Panels
License: All rights reserved
LicenseURL: http://en.wikipedia.org/wiki/All_rights_reserved
objects: PartDesign::CoordinateSystem×19, Sketcher::SketchObject×7, PartDesign::Pocket×3, PartDesign::Pad×2, PartDesign::Hole×2, Part::Part2DObjectPython×2, PartDesign::Body×2, PartDesign::Chamfer×1, PartDesign::Fillet×1
note: 48 computed .brp shape members not serialized (recipe doc carries the construction recipe); baked Part::Feature solids carry a one-line shape summary decoded from their .brp

FEATURE [Sketcher::SketchObject] Sketch001  label="Master_Sketch_Front"
  FullyConstrained = true
  MapMode = 5
  Placement = pos=(0,0,0) rot=(1,0,0;1.5708rad)
  Support = -> [XZ_Plane]
  sketch-geometry (38):
    g0: ArcOfCircle CenterX=-57.5 CenterY=-20.75 CenterZ=0 NormalX=0 NormalY=0 NormalZ=1 AngleXU=0 Radius=5 StartAngle=3.14159 EndAngle=4.71239
    g1: LineSegment StartX=-62.5 StartY=-20.75 StartZ=0 EndX=-62.5 EndY=20.75 EndZ=0
    g2: ArcOfCircle CenterX=-57.5 CenterY=20.75 CenterZ=0 NormalX=0 NormalY=0 NormalZ=1 AngleXU=0 Radius=5 StartAngle=1.5708 EndAngle=3.14159
    g3: LineSegment StartX=-57.5 StartY=25.75 StartZ=0 EndX=57.5 EndY=25.75 EndZ=0
    g4: ArcOfCircle CenterX=57.5 CenterY=20.75 CenterZ=0 NormalX=0 NormalY=0 NormalZ=1 AngleXU=0 Radius=5 StartAngle=3e-16 EndAngle=1.5708
    g5: LineSegment StartX=62.5 StartY=20.75 StartZ=0 EndX=62.5 EndY=-20.75 EndZ=0
    g6: ArcOfCircle CenterX=57.5 CenterY=-20.75 CenterZ=0 NormalX=0 NormalY=0 NormalZ=1 AngleXU=0 Radius=5 StartAngle=4.71239 EndAngle=6.28319
    g7: LineSegment StartX=57.5 StartY=-25.75 StartZ=0 EndX=-57.5 EndY=-25.75 EndZ=0
    g8: GeomPoint X=-62.5 Y=-25.75 Z=0
    g9: GeomPoint X=62.5 Y=25.75 Z=0
    g10: LineSegment StartX=-18 StartY=-9 StartZ=0 EndX=-18 EndY=9 EndZ=0
    g11: LineSegment StartX=-18 StartY=9 StartZ=0 EndX=18 EndY=9 EndZ=0
    g12: LineSegment StartX=18 StartY=9 StartZ=0 EndX=18 EndY=-9 EndZ=0
    g13: LineSegment StartX=18 StartY=-9 StartZ=0 EndX=-18 EndY=-9 EndZ=0
    g14: GeomPoint X=0 Y=0 Z=0
    g15: Circle CenterX=40 CenterY=0 CenterZ=0 NormalX=0 NormalY=0 NormalZ=1 AngleXU=0 Radius=3.6
    g16: ArcOfCircle CenterX=-40 CenterY=0 CenterZ=0 NormalX=0 NormalY=0 NormalZ=1 AngleXU=0 Radius=7.75 StartAngle=2.03937 EndAngle=7.38541
    g17: LineSegment StartX=-43.5 StartY=6.91466 StartZ=0 EndX=-43.5 EndY=10.5 EndZ=0
    g18: LineSegment StartX=-43.5 StartY=10.5 StartZ=0 EndX=-36.5 EndY=10.5 EndZ=0
    g19: LineSegment StartX=-36.5 StartY=10.5 StartZ=0 EndX=-36.5 EndY=6.91466 EndZ=0
    g20: LineSegment StartX=-57.75 StartY=-21.75 StartZ=0 EndX=-57.75 EndY=21.75 EndZ=0
    g21: LineSegment StartX=-57.75 StartY=21.75 StartZ=0 EndX=57.75 EndY=21.75 EndZ=0
    g22: LineSegment StartX=57.75 StartY=21.75 StartZ=0 EndX=57.75 EndY=-21.75 EndZ=0
    g23: LineSegment StartX=57.75 StartY=-21.75 StartZ=0 EndX=-57.75 EndY=-21.75 EndZ=0
    g24: GeomPoint X=-6e-16 Y=-2.7e-15 Z=0
    g25: Circle CenterX=-57.75 CenterY=21.75 CenterZ=0 NormalX=0 NormalY=0 NormalZ=1 AngleXU=0 Radius=2
    g26: Circle CenterX=57.75 CenterY=21.75 CenterZ=0 NormalX=0 NormalY=0 NormalZ=1 AngleXU=0 Radius=2
    g27: Circle CenterX=57.75 CenterY=-21.75 CenterZ=0 NormalX=0 NormalY=0 NormalZ=1 AngleXU=0 Radius=2
    g28: Circle CenterX=-57.75 CenterY=-21.75 CenterZ=0 NormalX=0 NormalY=0 NormalZ=1 AngleXU=0 Radius=2
    g29: LineSegment StartX=-47.25 StartY=-7.25 StartZ=0 EndX=-47.25 EndY=7.25 EndZ=0
    g30: LineSegment StartX=-47.25 StartY=7.25 StartZ=0 EndX=-32.75 EndY=7.25 EndZ=0
    g31: LineSegment StartX=-32.75 StartY=7.25 StartZ=0 EndX=-32.75 EndY=-7.25 EndZ=0
    g32: LineSegment StartX=-32.75 StartY=-7.25 StartZ=0 EndX=-47.25 EndY=-7.25 EndZ=0
    g33: GeomPoint X=-40 Y=0 Z=0
    g34: Circle CenterX=-47.25 CenterY=7.25 CenterZ=0 NormalX=0 NormalY=0 NormalZ=1 AngleXU=0 Radius=1.25
    g35: Circle CenterX=-32.75 CenterY=7.25 CenterZ=0 NormalX=0 NormalY=0 NormalZ=1 AngleXU=0 Radius=1.25
    g36: Circle CenterX=-47.25 CenterY=-7.25 CenterZ=0 NormalX=0 NormalY=0 NormalZ=1 AngleXU=0 Radius=1.25
    g37: Circle CenterX=-32.75 CenterY=-7.25 CenterZ=0 NormalX=0 NormalY=0 NormalZ=1 AngleXU=0 Radius=1.25
  constraints (90):
    c: Tangent(g0,g1) = 1.5708
    c: Tangent(g1,g2) = 1.5708
    c: Tangent(g2,g3) = 1.5708
    c: Tangent(g3,g4) = 1.5708
    c: Tangent(g4,g5) = 1.5708
    c: Tangent(g5,g6) = 1.5708
    c: Tangent(g6,g7) = 1.5708
    c: Tangent(g7,g0) = 1.5708
    c: Horizontal(g3)
    c: Horizontal(g7)
    c: Vertical(g1)
    c: Vertical(g5)
    c: Equal(g0,g2)
    c: Equal(g2,g4)
    c: Equal(g4,g6)
    c: PointOnObject(g8,g1)
    c: PointOnObject(g8,g7)
    c: PointOnObject(g9,g3)
    c: PointOnObject(g9,g5)
    c: Symmetric(g0,g4,g-1)
    c: Distance(g0,g5) = 125
    c: Distance(g0,g2) = 51.5
    c: Radius(g2) = 5
    c: Coincident(g10,g11)
    c: Coincident(g11,g12)
    c: Coincident(g12,g13)
    c: Coincident(g13,g10)
    c: Horizontal(g11)
    c: Horizontal(g13)
    c: Vertical(g10)
    c: Vertical(g12)
    c: Symmetric(g11,g10,g14)
    c: Coincident(g14,g-1)
    c: Distance(g11) = 36
    c: Distance(g10) = 18
    c: PointOnObject(g15,g-1)
    c: Coincident(g17,g18)
    c: Coincident(g18,g19)
    c: Coincident(g19,g16)
    c: Horizontal(g18)
    c: Vertical(g19)
    c: Vertical(g17)
    c: Horizontal(g17,g16)
    c: Coincident(g17,g16)
    c: Coincident(g20,g21)
    c: Coincident(g21,g22)
    c: Coincident(g22,g23)
    c: Coincident(g23,g20)
    c: Horizontal(g21)
    c: Horizontal(g23)
    c: Vertical(g20)
    c: Vertical(g22)
    c: Symmetric(g21,g20,g24)
    c: Coincident(g24,g-1)
    c: Coincident(g25,g20)
    c: Coincident(g26,g21)
    c: Coincident(g27,g22)
    c: Coincident(g28,g20)
    c: Equal(g28,g25)
    c: Equal(g25,g26)
    c: Equal(g26,g27)
    c: Diameter(g25) = 4
    c: Distance(g21) = 115.5
    c: Distance(g20) = 43.5
    c: Radius(g16) = 7.75
    c: DistanceY(g16,g17) = 10.5
    c: DistanceX(g18,g18) = 7
    c: Symmetric(g16,g15,g-2)
    c: Distance(g16,g15) = 80
    c: Diameter(g15) = 7.2
    c: Coincident(g29,g30)
    c: Coincident(g30,g31)
    c: Coincident(g31,g32)
    c: Coincident(g32,g29)
    c: Horizontal(g30)
    c: Horizontal(g32)
    c: Vertical(g29)
    c: Vertical(g31)
    c: Symmetric(g30,g29,g33)
    c: Coincident(g33,g16)
    c: Equal(g30,g31)
    c: Distance(g30) = 14.5
    c: Coincident(g34,g29)
    c: Coincident(g35,g30)
    c: Coincident(g36,g29)
    c: Coincident(g37,g31)
    c: Equal(g37,g36)
    c: Equal(g36,g35)
    c: Equal(g35,g34)
    c: Diameter(g34) = 2.5
FEATURE [Sketcher::SketchObject] Sketch
  FullyConstrained = true
  MapMode = 5
  Placement = pos=(0,0,0) rot=(1,0,0;1.5708rad)
  Support = -> [XZ_Plane]
  expr: Constraints[20] = Sketch001.Constraints[20]
  expr: Constraints[21] = Sketch001.Constraints[21]
  expr: Constraints[22] = Sketch001.Constraints[22]
  expr: Constraints[33] = Sketch001.Constraints[33]
  expr: Constraints[34] = Sketch001.Constraints[34]
  expr: Constraints[61] = Sketch001.Constraints[61]
  expr: Constraints[62] = Sketch001.Constraints[62]
  expr: Constraints[63] = Sketch001.Constraints[63]
  expr: Constraints[64] = Sketch001.Constraints[64]
  expr: Constraints[65] = Sketch001.Constraints[65]
  expr: Constraints[66] = Sketch001.Constraints[66]
  expr: Constraints[68] = Sketch001.Constraints[68]
  expr: Constraints[69] = Sketch001.Constraints[69]
  expr: Constraints[81] = Sketch001.Constraints[81]
  expr: Constraints[89] = Sketch001.Constraints[89]
  sketch-geometry (38):
    g0: ArcOfCircle CenterX=-57.5 CenterY=-20.75 CenterZ=0 NormalX=0 NormalY=0 NormalZ=1 AngleXU=0 Radius=5 StartAngle=3.14159 EndAngle=4.71239
    g1: LineSegment StartX=-62.5 StartY=-20.75 StartZ=0 EndX=-62.5 EndY=20.75 EndZ=0
    g2: ArcOfCircle CenterX=-57.5 CenterY=20.75 CenterZ=0 NormalX=0 NormalY=0 NormalZ=1 AngleXU=0 Radius=5 StartAngle=1.5708 EndAngle=3.14159
    g3: LineSegment StartX=-57.5 StartY=25.75 StartZ=0 EndX=57.5 EndY=25.75 EndZ=0
    g4: ArcOfCircle CenterX=57.5 CenterY=20.75 CenterZ=0 NormalX=0 NormalY=0 NormalZ=1 AngleXU=0 Radius=5 StartAngle=1e-16 EndAngle=1.5708
    g5: LineSegment StartX=62.5 StartY=20.75 StartZ=0 EndX=62.5 EndY=-20.75 EndZ=0
    g6: ArcOfCircle CenterX=57.5 CenterY=-20.75 CenterZ=0 NormalX=0 NormalY=0 NormalZ=1 AngleXU=0 Radius=5 StartAngle=4.71239 EndAngle=6.28319
    g7: LineSegment StartX=57.5 StartY=-25.75 StartZ=0 EndX=-57.5 EndY=-25.75 EndZ=0
    g8: GeomPoint X=-62.5 Y=-25.75 Z=0
    g9: GeomPoint X=62.5 Y=25.75 Z=0
    g10: LineSegment StartX=-18 StartY=-9 StartZ=0 EndX=-18 EndY=9 EndZ=0
    g11: LineSegment StartX=-18 StartY=9 StartZ=0 EndX=18 EndY=9 EndZ=0
    g12: LineSegment StartX=18 StartY=9 StartZ=0 EndX=18 EndY=-9 EndZ=0
    g13: LineSegment StartX=18 StartY=-9 StartZ=0 EndX=-18 EndY=-9 EndZ=0
    g14: GeomPoint X=0 Y=0 Z=0
    g15: Circle CenterX=40 CenterY=0 CenterZ=0 NormalX=0 NormalY=0 NormalZ=1 AngleXU=0 Radius=3.6
    g16: ArcOfCircle CenterX=-40 CenterY=0 CenterZ=0 NormalX=0 NormalY=0 NormalZ=1 AngleXU=0 Radius=7.75 StartAngle=2.03937 EndAngle=7.38541
    g17: LineSegment StartX=-43.5 StartY=6.91466 StartZ=0 EndX=-43.5 EndY=10.5 EndZ=0
    g18: LineSegment StartX=-43.5 StartY=10.5 StartZ=0 EndX=-36.5 EndY=10.5 EndZ=0
    g19: LineSegment StartX=-36.5 StartY=10.5 StartZ=0 EndX=-36.5 EndY=6.91466 EndZ=0
    g20: LineSegment StartX=-57.75 StartY=-21.75 StartZ=0 EndX=-57.75 EndY=21.75 EndZ=0
    g21: LineSegment StartX=-57.75 StartY=21.75 StartZ=0 EndX=57.75 EndY=21.75 EndZ=0
    g22: LineSegment StartX=57.75 StartY=21.75 StartZ=0 EndX=57.75 EndY=-21.75 EndZ=0
    g23: LineSegment StartX=57.75 StartY=-21.75 StartZ=0 EndX=-57.75 EndY=-21.75 EndZ=0
    g24: GeomPoint X=-6e-16 Y=-2.7e-15 Z=0
    g25: Circle CenterX=-57.75 CenterY=21.75 CenterZ=0 NormalX=0 NormalY=0 NormalZ=1 AngleXU=0 Radius=2
    g26: Circle CenterX=57.75 CenterY=21.75 CenterZ=0 NormalX=0 NormalY=0 NormalZ=1 AngleXU=0 Radius=2
    g27: Circle CenterX=57.75 CenterY=-21.75 CenterZ=0 NormalX=0 NormalY=0 NormalZ=1 AngleXU=0 Radius=2
    g28: Circle CenterX=-57.75 CenterY=-21.75 CenterZ=0 NormalX=0 NormalY=0 NormalZ=1 AngleXU=0 Radius=2
    g29: LineSegment StartX=-47.25 StartY=-7.25 StartZ=0 EndX=-47.25 EndY=7.25 EndZ=0
    g30: LineSegment StartX=-47.25 StartY=7.25 StartZ=0 EndX=-32.75 EndY=7.25 EndZ=0
    g31: LineSegment StartX=-32.75 StartY=7.25 StartZ=0 EndX=-32.75 EndY=-7.25 EndZ=0
    g32: LineSegment StartX=-32.75 StartY=-7.25 StartZ=0 EndX=-47.25 EndY=-7.25 EndZ=0
    g33: GeomPoint X=-40 Y=0 Z=0
    g34: Circle CenterX=-47.25 CenterY=7.25 CenterZ=0 NormalX=0 NormalY=0 NormalZ=1 AngleXU=0 Radius=1.25
    g35: Circle CenterX=-32.75 CenterY=7.25 CenterZ=0 NormalX=0 NormalY=0 NormalZ=1 AngleXU=0 Radius=1.25
    g36: Circle CenterX=-47.25 CenterY=-7.25 CenterZ=0 NormalX=0 NormalY=0 NormalZ=1 AngleXU=0 Radius=1.25
    g37: Circle CenterX=-32.75 CenterY=-7.25 CenterZ=0 NormalX=0 NormalY=0 NormalZ=1 AngleXU=0 Radius=1.25
  constraints (90):
    c: Tangent(g0,g1) = 1.5708
    c: Tangent(g1,g2) = 1.5708
    c: Tangent(g2,g3) = 1.5708
    c: Tangent(g3,g4) = 1.5708
    c: Tangent(g4,g5) = 1.5708
    c: Tangent(g5,g6) = 1.5708
    c: Tangent(g6,g7) = 1.5708
    c: Tangent(g7,g0) = 1.5708
    c: Horizontal(g3)
    c: Horizontal(g7)
    c: Vertical(g1)
    c: Vertical(g5)
    c: Equal(g0,g2)
    c: Equal(g2,g4)
    c: Equal(g4,g6)
    c: PointOnObject(g8,g1)
    c: PointOnObject(g8,g7)
    c: PointOnObject(g9,g3)
    c: PointOnObject(g9,g5)
    c: Symmetric(g0,g4,g-1)
    c: Distance(g0,g5) = 125
    c: Distance(g0,g2) = 51.5
    c: Radius(g2) = 5
    c: Coincident(g10,g11)
    c: Coincident(g11,g12)
    c: Coincident(g12,g13)
    c: Coincident(g13,g10)
    c: Horizontal(g11)
    c: Horizontal(g13)
    c: Vertical(g10)
    c: Vertical(g12)
    c: Symmetric(g11,g10,g14)
    c: Coincident(g14,g-1)
    c: Distance(g11) = 36
    c: Distance(g10) = 18
    c: PointOnObject(g15,g-1)
    c: Coincident(g17,g18)
    c: Coincident(g18,g19)
    c: Coincident(g19,g16)
    c: Horizontal(g18)
    c: Vertical(g19)
    c: Vertical(g17)
    c: Horizontal(g17,g16)
    c: Coincident(g17,g16)
    c: Coincident(g20,g21)
    c: Coincident(g21,g22)
    c: Coincident(g22,g23)
    c: Coincident(g23,g20)
    c: Horizontal(g21)
    c: Horizontal(g23)
    c: Vertical(g20)
    c: Vertical(g22)
    c: Symmetric(g21,g20,g24)
    c: Coincident(g24,g-1)
    c: Coincident(g25,g20)
    c: Coincident(g26,g21)
    c: Coincident(g27,g22)
    c: Coincident(g28,g20)
    c: Equal(g28,g25)
    c: Equal(g25,g26)
    c: Equal(g26,g27)
    c: Diameter(g25) = 4
    c: Distance(g21) = 115.5
    c: Distance(g20) = 43.5
    c: Radius(g16) = 7.75
    c: DistanceY(g16,g17) = 10.5
    c: DistanceX(g18,g18) = 7
    c: Symmetric(g16,g15,g-2)
    c: Distance(g16,g15) = 80
    c: Diameter(g15) = 7.2
    c: Coincident(g29,g30)
    c: Coincident(g30,g31)
    c: Coincident(g31,g32)
    c: Coincident(g32,g29)
    c: Horizontal(g30)
    c: Horizontal(g32)
    c: Vertical(g29)
    c: Vertical(g31)
    c: Symmetric(g30,g29,g33)
    c: Coincident(g33,g16)
    c: Equal(g30,g31)
    c: Distance(g30) = 14.5
    c: Coincident(g34,g29)
    c: Coincident(g35,g30)
    c: Coincident(g36,g29)
    c: Coincident(g37,g31)
    c: Equal(g37,g36)
    c: Equal(g36,g35)
    c: Equal(g35,g34)
    c: Diameter(g34) = 2.5
FEATURE [PartDesign::Pad] Pad
  Direction = (0,-1,-2e-16)
  Length = 4
  Length2 = 10
  Placement = pos=(0,0,0) rot=(1,0,0;1.5708rad)
  Profile = -> Sketch
  ReferenceAxis = -> Sketch [N_Axis]
  Refine = true
  Type = 0
FEATURE [Sketcher::SketchObject] Sketch002
  AttachmentOffset = pos=(0,0,4) rot=(0,0,1;0rad)
  FullyConstrained = true
  MapMode = 5
  Placement = pos=(0,-4,-9e-16) rot=(1,0,0;1.5708rad)
  Support = -> [XZ_Plane]
  expr: Constraints[20] = Sketch001.Constraints[20]
  expr: Constraints[21] = Sketch001.Constraints[21]
  expr: Constraints[22] = Sketch001.Constraints[22]
  expr: Constraints[33] = Sketch001.Constraints[33]
  expr: Constraints[34] = Sketch001.Constraints[34]
  expr: Constraints[61] = Sketch001.Constraints[61]
  expr: Constraints[62] = Sketch001.Constraints[62]
  expr: Constraints[63] = Sketch001.Constraints[63]
  expr: Constraints[64] = Sketch001.Constraints[64]
  expr: Constraints[65] = Sketch001.Constraints[65]
  expr: Constraints[66] = Sketch001.Constraints[66]
  expr: Constraints[68] = Sketch001.Constraints[68]
  expr: Constraints[69] = Sketch001.Constraints[69]
  expr: Constraints[81] = Sketch001.Constraints[81]
  expr: Constraints[89] = Sketch001.Constraints[89]
  sketch-geometry (38):
    g0: ArcOfCircle CenterX=-57.5 CenterY=-20.75 CenterZ=0 NormalX=0 NormalY=0 NormalZ=1 AngleXU=0 Radius=5 StartAngle=3.14159 EndAngle=4.71239
    g1: LineSegment StartX=-62.5 StartY=-20.75 StartZ=0 EndX=-62.5 EndY=20.75 EndZ=0
    g2: ArcOfCircle CenterX=-57.5 CenterY=20.75 CenterZ=0 NormalX=0 NormalY=0 NormalZ=1 AngleXU=0 Radius=5 StartAngle=1.5708 EndAngle=3.14159
    g3: LineSegment StartX=-57.5 StartY=25.75 StartZ=0 EndX=57.5 EndY=25.75 EndZ=0
    g4: ArcOfCircle CenterX=57.5 CenterY=20.75 CenterZ=0 NormalX=0 NormalY=0 NormalZ=1 AngleXU=0 Radius=5 StartAngle=0 EndAngle=1.5708
    g5: LineSegment StartX=62.5 StartY=20.75 StartZ=0 EndX=62.5 EndY=-20.75 EndZ=0
    g6: ArcOfCircle CenterX=57.5 CenterY=-20.75 CenterZ=0 NormalX=0 NormalY=0 NormalZ=1 AngleXU=0 Radius=5 StartAngle=4.71239 EndAngle=6.28319
    g7: LineSegment StartX=57.5 StartY=-25.75 StartZ=0 EndX=-57.5 EndY=-25.75 EndZ=0
    g8: GeomPoint X=-62.5 Y=-25.75 Z=0
    g9: GeomPoint X=62.5 Y=25.75 Z=0
    g10: LineSegment StartX=-18 StartY=-9 StartZ=0 EndX=-18 EndY=9 EndZ=0
    g11: LineSegment StartX=-18 StartY=9 StartZ=0 EndX=18 EndY=9 EndZ=0
    g12: LineSegment StartX=18 StartY=9 StartZ=0 EndX=18 EndY=-9 EndZ=0
    g13: LineSegment StartX=18 StartY=-9 StartZ=0 EndX=-18 EndY=-9 EndZ=0
    g14: GeomPoint X=0 Y=0 Z=0
    g15: Circle CenterX=40 CenterY=0 CenterZ=0 NormalX=0 NormalY=0 NormalZ=1 AngleXU=0 Radius=3.6
    g16: ArcOfCircle CenterX=-40 CenterY=0 CenterZ=0 NormalX=0 NormalY=0 NormalZ=1 AngleXU=0 Radius=7.75 StartAngle=2.03937 EndAngle=7.38541
    g17: LineSegment StartX=-43.5 StartY=6.91466 StartZ=0 EndX=-43.5 EndY=10.5 EndZ=0
    g18: LineSegment StartX=-43.5 StartY=10.5 StartZ=0 EndX=-36.5 EndY=10.5 EndZ=0
    g19: LineSegment StartX=-36.5 StartY=10.5 StartZ=0 EndX=-36.5 EndY=6.91466 EndZ=0
    g20: LineSegment StartX=-57.75 StartY=-21.75 StartZ=0 EndX=-57.75 EndY=21.75 EndZ=0
    g21: LineSegment StartX=-57.75 StartY=21.75 StartZ=0 EndX=57.75 EndY=21.75 EndZ=0
    g22: LineSegment StartX=57.75 StartY=21.75 StartZ=0 EndX=57.75 EndY=-21.75 EndZ=0
    g23: LineSegment StartX=57.75 StartY=-21.75 StartZ=0 EndX=-57.75 EndY=-21.75 EndZ=0
    g24: GeomPoint X=-6e-16 Y=-2.7e-15 Z=0
    g25: Circle CenterX=-57.75 CenterY=21.75 CenterZ=0 NormalX=0 NormalY=0 NormalZ=1 AngleXU=0 Radius=2
    g26: Circle CenterX=57.75 CenterY=21.75 CenterZ=0 NormalX=0 NormalY=0 NormalZ=1 AngleXU=0 Radius=2
    g27: Circle CenterX=57.75 CenterY=-21.75 CenterZ=0 NormalX=0 NormalY=0 NormalZ=1 AngleXU=0 Radius=2
    g28: Circle CenterX=-57.75 CenterY=-21.75 CenterZ=0 NormalX=0 NormalY=0 NormalZ=1 AngleXU=0 Radius=2
    g29: LineSegment StartX=-47.25 StartY=-7.25 StartZ=0 EndX=-47.25 EndY=7.25 EndZ=0
    g30: LineSegment StartX=-47.25 StartY=7.25 StartZ=0 EndX=-32.75 EndY=7.25 EndZ=0
    g31: LineSegment StartX=-32.75 StartY=7.25 StartZ=0 EndX=-32.75 EndY=-7.25 EndZ=0
    g32: LineSegment StartX=-32.75 StartY=-7.25 StartZ=0 EndX=-47.25 EndY=-7.25 EndZ=0
    g33: GeomPoint X=-40 Y=0 Z=0
    g34: Circle CenterX=-47.25 CenterY=7.25 CenterZ=0 NormalX=0 NormalY=0 NormalZ=1 AngleXU=0 Radius=1.25
    g35: Circle CenterX=-32.75 CenterY=7.25 CenterZ=0 NormalX=0 NormalY=0 NormalZ=1 AngleXU=0 Radius=1.25
    g36: Circle CenterX=-47.25 CenterY=-7.25 CenterZ=0 NormalX=0 NormalY=0 NormalZ=1 AngleXU=0 Radius=1.25
    g37: Circle CenterX=-32.75 CenterY=-7.25 CenterZ=0 NormalX=0 NormalY=0 NormalZ=1 AngleXU=0 Radius=1.25
  constraints (90):
    c: Tangent(g0,g1) = 1.5708
    c: Tangent(g1,g2) = 1.5708
    c: Tangent(g2,g3) = 1.5708
    c: Tangent(g3,g4) = 1.5708
    c: Tangent(g4,g5) = 1.5708
    c: Tangent(g5,g6) = 1.5708
    c: Tangent(g6,g7) = 1.5708
    c: Tangent(g7,g0) = 1.5708
    c: Horizontal(g3)
    c: Horizontal(g7)
    c: Vertical(g1)
    c: Vertical(g5)
    c: Equal(g0,g2)
    c: Equal(g2,g4)
    c: Equal(g4,g6)
    c: PointOnObject(g8,g1)
    c: PointOnObject(g8,g7)
    c: PointOnObject(g9,g3)
    c: PointOnObject(g9,g5)
    c: Symmetric(g0,g4,g-1)
    c: Distance(g0,g5) = 125
    c: Distance(g0,g2) = 51.5
    c: Radius(g2) = 5
    c: Coincident(g10,g11)
    c: Coincident(g11,g12)
    c: Coincident(g12,g13)
    c: Coincident(g13,g10)
    c: Horizontal(g11)
    c: Horizontal(g13)
    c: Vertical(g10)
    c: Vertical(g12)
    c: Symmetric(g11,g10,g14)
    c: Coincident(g14,g-1)
    c: Distance(g11) = 36
    c: Distance(g10) = 18
    c: PointOnObject(g15,g-1)
    c: Coincident(g17,g18)
    c: Coincident(g18,g19)
    c: Coincident(g19,g16)
    c: Horizontal(g18)
    c: Vertical(g19)
    c: Vertical(g17)
    c: Horizontal(g17,g16)
    c: Coincident(g17,g16)
    c: Coincident(g20,g21)
    c: Coincident(g21,g22)
    c: Coincident(g22,g23)
    c: Coincident(g23,g20)
    c: Horizontal(g21)
    c: Horizontal(g23)
    c: Vertical(g20)
    c: Vertical(g22)
    c: Symmetric(g21,g20,g24)
    c: Coincident(g24,g-1)
    c: Coincident(g25,g20)
    c: Coincident(g26,g21)
    c: Coincident(g27,g22)
    c: Coincident(g28,g20)
    c: Equal(g28,g25)
    c: Equal(g25,g26)
    c: Equal(g26,g27)
    c: Diameter(g25) = 4
    c: Distance(g21) = 115.5
    c: Distance(g20) = 43.5
    c: Radius(g16) = 7.75
    c: DistanceY(g16,g17) = 10.5
    c: DistanceX(g18,g18) = 7
    c: Symmetric(g16,g15,g-2)
    c: Distance(g16,g15) = 80
    c: Diameter(g15) = 7.2
    c: Coincident(g29,g30)
    c: Coincident(g30,g31)
    c: Coincident(g31,g32)
    c: Coincident(g32,g29)
    c: Horizontal(g30)
    c: Horizontal(g32)
    c: Vertical(g29)
    c: Vertical(g31)
    c: Symmetric(g30,g29,g33)
    c: Coincident(g33,g16)
    c: Equal(g30,g31)
    c: Distance(g30) = 14.5
    c: Coincident(g34,g29)
    c: Coincident(g35,g30)
    c: Coincident(g36,g29)
    c: Coincident(g37,g31)
    c: Equal(g37,g36)
    c: Equal(g36,g35)
    c: Equal(g35,g34)
    c: Diameter(g34) = 2.5
FEATURE [PartDesign::Hole] Hole
  BaseFeature = -> Pad
  CustomThreadClearance = 0
  Depth = 25
  DepthType = 0
  Diameter = 3.2
  DrillForDepth = false
  DrillPoint = 1
  DrillPointAngle = 118
  HoleCutCountersinkAngle = 90
  HoleCutCustomValues = false
  HoleCutDepth = 0
  HoleCutDiameter = 4.64
  HoleCutType = 0
  ModelThread = false
  Placement = pos=(0,0,0) rot=(1,0,0;1.5708rad)
  Profile = -> Sketch002
  Refine = true
  Tapered = false
  TaperedAngle = 90
  ThreadClass = 0
  ThreadDepth = 25
  ThreadDepthType = 0
  ThreadDirection = 0
  ThreadFit = 1
  ThreadSize = 9
  ThreadType = 1
  Threaded = false
  UseCustomThreadClearance = false
FEATURE [PartDesign::Chamfer] Chamfer
  Angle = 45
  Base = -> Hole [Edge41,Edge43,Edge44,Edge42]
  BaseFeature = -> Hole
  ChamferType = 0
  FlipDirection = false
  Placement = pos=(0,0,0) rot=(1,0,0;1.5708rad)
  Refine = true
  Size = 3.5
  Size2 = 1
  SupportTransform = false
  UseAllEdges = false
FEATURE [PartDesign::Fillet] Fillet
  Base = -> Chamfer [Edge59,Edge58]
  BaseFeature = -> Chamfer
  Placement = pos=(0,0,0) rot=(1,0,0;1.5708rad)
  Radius = 1
  Refine = true
  SupportTransform = false
  UseAllEdges = false
FEATURE [Sketcher::SketchObject] Sketch003  label="Sketch_Pad"
  FullyConstrained = true
  MapMode = 5
  Placement = pos=(0,0,0) rot=(1,0,0;1.5708rad)
  Support = -> [XZ_Plane001]
  expr: Constraints[20] = Sketch001.Constraints[20]
  expr: Constraints[21] = Sketch001.Constraints[21]
  expr: Constraints[22] = Sketch001.Constraints[22]
  expr: Constraints[38] = Sketch001.Constraints[61]
  expr: Constraints[39] = Sketch001.Constraints[62]
  expr: Constraints[40] = Sketch001.Constraints[63]
  sketch-geometry (36):
    g0: ArcOfCircle CenterX=-57.5 CenterY=-20.75 CenterZ=0 NormalX=0 NormalY=0 NormalZ=1 AngleXU=0 Radius=5 StartAngle=3.14159 EndAngle=4.71239
    g1: LineSegment StartX=-62.5 StartY=-20.75 StartZ=0 EndX=-62.5 EndY=20.75 EndZ=0
    g2: ArcOfCircle CenterX=-57.5 CenterY=20.75 CenterZ=0 NormalX=0 NormalY=0 NormalZ=1 AngleXU=0 Radius=5 StartAngle=1.5708 EndAngle=3.14159
    g3: LineSegment StartX=-57.5 StartY=25.75 StartZ=0 EndX=57.5 EndY=25.75 EndZ=0
    g4: ArcOfCircle CenterX=57.5 CenterY=20.75 CenterZ=0 NormalX=0 NormalY=0 NormalZ=1 AngleXU=0 Radius=5 StartAngle=4e-16 EndAngle=1.5708
    g5: LineSegment StartX=62.5 StartY=20.75 StartZ=0 EndX=62.5 EndY=-20.75 EndZ=0
    g6: ArcOfCircle CenterX=57.5 CenterY=-20.75 CenterZ=0 NormalX=0 NormalY=0 NormalZ=1 AngleXU=0 Radius=5 StartAngle=4.71239 EndAngle=6.28319
    g7: LineSegment StartX=57.5 StartY=-25.75 StartZ=0 EndX=-57.5 EndY=-25.75 EndZ=0
    g8: GeomPoint X=-62.5 Y=-25.75 Z=0
    g9: GeomPoint X=62.5 Y=25.75 Z=0
    g10: LineSegment StartX=-57.75 StartY=-21.75 StartZ=0 EndX=-57.75 EndY=21.75 EndZ=0
    g11: LineSegment StartX=-57.75 StartY=21.75 StartZ=0 EndX=57.75 EndY=21.75 EndZ=0
    g12: LineSegment StartX=57.75 StartY=21.75 StartZ=0 EndX=57.75 EndY=-21.75 EndZ=0
    g13: LineSegment StartX=57.75 StartY=-21.75 StartZ=0 EndX=-57.75 EndY=-21.75 EndZ=0
    g14: Circle CenterX=-57.75 CenterY=21.75 CenterZ=0 NormalX=0 NormalY=0 NormalZ=1 AngleXU=0 Radius=2
    g15: Circle CenterX=57.75 CenterY=21.75 CenterZ=0 NormalX=0 NormalY=0 NormalZ=1 AngleXU=0 Radius=2
    g16: Circle CenterX=57.75 CenterY=-21.75 CenterZ=0 NormalX=0 NormalY=0 NormalZ=1 AngleXU=0 Radius=2
    g17: Circle CenterX=-57.75 CenterY=-21.75 CenterZ=0 NormalX=0 NormalY=0 NormalZ=1 AngleXU=0 Radius=2
    g18: LineSegment StartX=39.6 StartY=19.45 StartZ=0 EndX=20.4 EndY=19.45 EndZ=0
    g19: LineSegment StartX=20.4 StartY=19.45 StartZ=0 EndX=20.4 EndY=6.55 EndZ=0
    g20: LineSegment StartX=20.4 StartY=6.55 StartZ=0 EndX=39.6 EndY=6.55 EndZ=0
    g21: LineSegment StartX=39.6 StartY=6.55 StartZ=0 EndX=39.6 EndY=19.45 EndZ=0
    g22: LineSegment StartX=39 StartY=0 StartZ=0 EndX=21 EndY=0 EndZ=0
    g23: LineSegment StartX=21 StartY=0 StartZ=0 EndX=16 EndY=-5 EndZ=0
    g24: LineSegment StartX=16 StartY=-5 StartZ=0 EndX=16 EndY=-17 EndZ=0
    g25: LineSegment StartX=19 StartY=-20 StartZ=0 EndX=41 EndY=-20 EndZ=0
    g26: LineSegment StartX=44 StartY=-17 StartZ=0 EndX=44 EndY=-5 EndZ=0
    g27: LineSegment StartX=44 StartY=-5 StartZ=0 EndX=39 EndY=0 EndZ=0
    g28: ArcOfCircle CenterX=19 CenterY=-17 CenterZ=0 NormalX=0 NormalY=0 NormalZ=1 AngleXU=0 Radius=3 StartAngle=3.14159 EndAngle=4.71239
    g29: ArcOfCircle CenterX=41 CenterY=-17 CenterZ=0 NormalX=0 NormalY=0 NormalZ=1 AngleXU=0 Radius=3 StartAngle=4.71239 EndAngle=6.28319
    g30: Circle CenterX=10 CenterY=-10 CenterZ=0 NormalX=0 NormalY=0 NormalZ=1 AngleXU=0 Radius=1.6
    g31: Circle CenterX=50 CenterY=-10 CenterZ=0 NormalX=0 NormalY=0 NormalZ=1 AngleXU=0 Radius=1.6
    g32: GeomPoint X=30 Y=2e-16 Z=0
    g33: GeomPoint X=30 Y=-20 Z=0
    g34: GeomPoint X=30 Y=-10 Z=0
    g35: GeomPoint X=30 Y=13 Z=0
  constraints (85):
    c: Tangent(g0,g1) = 1.5708
    c: Tangent(g1,g2) = 1.5708
    c: Tangent(g2,g3) = 1.5708
    c: Tangent(g3,g4) = 1.5708
    c: Tangent(g4,g5) = 1.5708
    c: Tangent(g5,g6) = 1.5708
    c: Tangent(g6,g7) = 1.5708
    c: Tangent(g7,g0) = 1.5708
    c: Horizontal(g3)
    c: Horizontal(g7)
    c: Vertical(g1)
    c: Vertical(g5)
    c: Equal(g0,g2)
    c: Equal(g2,g4)
    c: Equal(g4,g6)
    c: PointOnObject(g8,g1)
    c: PointOnObject(g8,g7)
    c: PointOnObject(g9,g3)
    c: PointOnObject(g9,g5)
    c: Symmetric(g0,g4,g-1)
    c: Distance(g0,g5) = 125
    c: Distance(g0,g2) = 51.5
    c: Radius(g2) = 5
    c: Coincident(g10,g11)
    c: Coincident(g11,g12)
    c: Coincident(g12,g13)
    c: Coincident(g13,g10)
    c: Horizontal(g11)
    c: Horizontal(g13)
    c: Vertical(g10)
    c: Vertical(g12)
    c: Coincident(g14,g10)
    c: Coincident(g15,g11)
    c: Coincident(g16,g12)
    c: Coincident(g17,g10)
    c: Equal(g17,g14)
    c: Equal(g14,g15)
    c: Equal(g15,g16)
    c: Diameter(g14) = 4
    c: Distance(g11) = 115.5
    c: Distance(g10) = 43.5
    c: Symmetric(g17,g15,g-1)
    c: Coincident(g18,g19)
    c: Coincident(g19,g20)
    c: Coincident(g20,g21)
    c: Coincident(g21,g18)
    c: Horizontal(g18)
    c: Horizontal(g20)
    c: Vertical(g19)
    c: Vertical(g21)
    c: Horizontal(g22)
    c: Coincident(g22,g23)
    c: Coincident(g23,g24)
    c: Vertical(g24)
    c: Horizontal(g25)
    c: Coincident(g26,g27)
    c: Coincident(g27,g22)
    c: Vertical(g26)
    c: Tangent(g24,g28) = -1.5708
    c: Tangent(g25,g28) = -1.5708
    c: Tangent(g25,g29) = -1.5708
    c: Tangent(g26,g29) = -1.5708
    c: Equal(g29,g28)
    c: Horizontal(g26,g23)
    c: Equal(g23,g27)
    c: DistanceX(g23,g26) = 28
    c: DistanceX(g18,g18) = 19.2
    c: DistanceY(g19,g19) = 12.9
    c: Equal(g31,g30)
    c: DistanceX(g30,g31) = 40
    c: Diameter(g30) = 3.2
    c: DistanceY(g25,g22) = 20
    c: Radius(g28) = 3
    c: DistanceX(g23,g22) = 5
    c: DistanceY(g23,g22) = 5
    c: Symmetric(g22,g22,g32)
    c: Symmetric(g25,g25,g33)
    c: Symmetric(g33,g32,g34)
    c: Symmetric(g30,g31,g34)
    c: Symmetric(g19,g18,g35)
    c: Vertical(g35,g34)
    c: DistanceX(g-1,g34) = 30  'SwitchOffset'
    c: DistanceY(g-1,g35) = 13  'SwitchHeight'
    c: DistanceY(g34,g-1) = 10
    c: Horizontal(g31,g30)
FEATURE [PartDesign::Pad] Pad001
  Direction = (0,-1,-2e-16)
  Length = 4
  Length2 = 10
  Placement = pos=(0,0,0) rot=(1,0,0;1.5708rad)
  Profile = -> Sketch003
  ReferenceAxis = -> Sketch003 [N_Axis]
  Refine = true
  Type = 0
FEATURE [Sketcher::SketchObject] Sketch004
  AttachmentOffset = pos=(0,0,4) rot=(0,0,1;0rad)
  FullyConstrained = true
  MapMode = 5
  Placement = pos=(0,-4,-9e-16) rot=(1,0,0;1.5708rad)
  Support = -> [XZ_Plane001]
  sketch-geometry (2):
    g0: Circle CenterX=-47.5 CenterY=-15 CenterZ=0 NormalX=0 NormalY=0 NormalZ=1 AngleXU=0 Radius=4
    g1: Circle CenterX=-47.5 CenterY=15 CenterZ=0 NormalX=0 NormalY=0 NormalZ=1 AngleXU=0 Radius=4
  constraints (5):
    c: DistanceX(g0,g-1) = 47.5
    c: DistanceY(g0,g-1) = 15
    c: Diameter(g0) = 8
    c: Equal(g1,g0)
    c: Symmetric(g1,g0,g-1)
FEATURE [PartDesign::Hole] Hole001
  BaseFeature = -> Pad001
  CustomThreadClearance = 0
  Depth = 25
  DepthType = 0
  Diameter = 8
  DrillForDepth = false
  DrillPoint = 0
  DrillPointAngle = 118
  HoleCutCountersinkAngle = 90
  HoleCutCustomValues = false
  HoleCutDepth = 2
  HoleCutDiameter = 10
  HoleCutType = 1
  ModelThread = false
  Placement = pos=(0,0,0) rot=(1,0,0;1.5708rad)
  Profile = -> Sketch004
  Refine = true
  Tapered = false
  TaperedAngle = 90
  ThreadClass = 0
  ThreadDepth = 25
  ThreadDepthType = 0
  ThreadDirection = 0
  ThreadFit = 0
  ThreadSize = 0
  ThreadType = 0
  Threaded = false
  UseCustomThreadClearance = false
FEATURE [Sketcher::SketchObject] Sketch005
  FullyConstrained = true
  MapMode = 5
  Placement = pos=(0,0,0) rot=(1,0,0;1.5708rad)
  Support = -> [XZ_Plane001]
  expr: Constraints[11] = <<Sketch_Pad>>.Constraints.SwitchOffset
  expr: Constraints[12] = <<Sketch_Pad>>.Constraints.SwitchHeight
  sketch-geometry (5):
    g0: LineSegment StartX=17.5 StartY=18 StartZ=0 EndX=42.5 EndY=18 EndZ=0
    g1: LineSegment StartX=42.5 StartY=18 StartZ=0 EndX=42.5 EndY=8 EndZ=0
    g2: LineSegment StartX=42.5 StartY=8 StartZ=0 EndX=17.5 EndY=8 EndZ=0
    g3: LineSegment StartX=17.5 StartY=8 StartZ=0 EndX=17.5 EndY=18 EndZ=0
    g4: GeomPoint X=30 Y=13 Z=0
  constraints (13):
    c: Coincident(g0,g1)
    c: Coincident(g1,g2)
    c: Coincident(g2,g3)
    c: Coincident(g3,g0)
    c: Horizontal(g0)
    c: Horizontal(g2)
    c: Vertical(g1)
    c: Vertical(g3)
    c: DistanceY(g3,g3) = 10
    c: DistanceX(g0,g0) = 25
    c: Symmetric(g2,g0,g4)
    c: DistanceX(g-1,g4) = 30
    c: DistanceY(g-1,g4) = 13
FEATURE [PartDesign::Pocket] Pocket
  BaseFeature = -> Hole001
  Direction = (0,1,2e-16)
  Length = 2
  Length2 = 5
  Placement = pos=(0,0,0) rot=(1,0,0;1.5708rad)
  Profile = -> Sketch005
  ReferenceAxis = -> Sketch005 [N_Axis]
  Refine = true
  Reversed = true
  Type = 0
FEATURE [Sketcher::SketchObject] Sketch006
  AttachmentOffset = pos=(0,0,4) rot=(0,0,1;0rad)
  ExternalGeometry = -> [Pocket]
  FullyConstrained = true
  MapMode = 5
  Placement = pos=(0,-4,-9e-16) rot=(1,0,0;1.5708rad)
  Support = -> [XZ_Plane001]
  expr: Constraints[7] = .Constraints.TextOffset
  sketch-geometry (2):
    g0: LineSegment StartX=-41.5 StartY=-16.88 StartZ=0 EndX=-21.5 EndY=-16.88 EndZ=0
    g1: LineSegment StartX=-41.5 StartY=13.12 StartZ=0 EndX=-21.5 EndY=13.12 EndZ=0
  constraints (8):
    c: Horizontal(g0)
    c: DistanceX(g-3,g0) = 6
    c: DistanceX(g0,g0) = 20
    c: DistanceY(g0,g-3) = 1.88  'TextOffset'
    c: Horizontal(g1)
    c: Equal(g1,g0)
    c: Vertical(g1,g0)
    c: DistanceY(g1,g-4) = 1.88
FEATURE [Part::Part2DObjectPython] ShapeString  # Draft 2D object (typed FeaturePython)
  AttachmentOffset = pos=(0,0,0) rot=(0,1,0;1.5708rad)
  FontFile = <path>
  MakeFace = true
  MapMode = 7
  Placement = pos=(-41.5,-4,-16.88) rot=(1,0,0;1.5708rad)
  Size = 4
  String = Stand
  Support = -> [Sketch006]
  Tracking = 0
FEATURE [PartDesign::Pocket] Pocket001
  BaseFeature = -> Pocket
  Direction = (2e-16,1,0)
  Length = 1
  Length2 = 5
  Placement = pos=(0,0,0) rot=(1,0,0;1.5708rad)
  Profile = -> ShapeString
  ReferenceAxis = -> ShapeString [N_Axis]
  Refine = true
  Type = 0
FEATURE [Part::Part2DObjectPython] ShapeString001  # Draft 2D object (typed FeaturePython)
  AttachmentOffset = pos=(0,0,0) rot=(0,1,0;1.5708rad)
  FontFile = <path>
  MakeFace = true
  MapMode = 1
  Placement = pos=(-41.5,-4,13.12) rot=(1,0,0;1.5708rad)
  Size = 4
  String = ST-link
  Support = -> [Sketch006]
  Tracking = 0
FEATURE [PartDesign::Pocket] Pocket002
  BaseFeature = -> Pocket001
  Direction = (0,1,-2e-16)
  Length = 1
  Length2 = 5
  Placement = pos=(0,0,0) rot=(1,0,0;1.5708rad)
  Profile = -> ShapeString001
  ReferenceAxis = -> ShapeString001 [N_Axis]
  Refine = true
  Type = 0
FEATURE [PartDesign::CoordinateSystem] LCS_PCBA_Mount
  AttacherType = Attacher::AttachEngine3D
  MapMode = 11
  Placement = pos=(40,0,0) rot=(0.57735,-0.57735,0.57735;2.0944rad)
  Support = -> [Fillet]
FEATURE [PartDesign::CoordinateSystem] LCS_Front_Hole_1_Top
  AttacherType = Attacher::AttachEngine3D
  MapMode = 11
  Placement = pos=(-57.75,-4,21.75) rot=(0.57735,-0.57735,0.57735;2.0944rad)
  Support = -> [Fillet]
FEATURE [PartDesign::CoordinateSystem] LCS_Front_Hole_2_Top
  AttacherType = Attacher::AttachEngine3D
  MapMode = 11
  Placement = pos=(57.75,-4,21.75) rot=(0.57735,-0.57735,0.57735;2.0944rad)
  Support = -> [Fillet]
FEATURE [PartDesign::CoordinateSystem] LCS_Front_Hole_3_Top
  AttacherType = Attacher::AttachEngine3D
  MapMode = 11
  Placement = pos=(57.75,-4,-21.75) rot=(0.57735,-0.57735,0.57735;2.0944rad)
  Support = -> [Fillet]
FEATURE [PartDesign::CoordinateSystem] LCS_Front_Hole_4_Top
  AttacherType = Attacher::AttachEngine3D
  MapMode = 11
  Placement = pos=(-57.75,-4,-21.75) rot=(0.57735,-0.57735,0.57735;2.0944rad)
  Support = -> [Fillet]
FEATURE [PartDesign::CoordinateSystem] LCS_Front_Hole_1_Bottom
  AttacherType = Attacher::AttachEngine3D
  MapMode = 11
  Placement = pos=(-57.75,0,21.75) rot=(0.57735,-0.57735,0.57735;2.0944rad)
  Support = -> [Fillet]
FEATURE [PartDesign::CoordinateSystem] LCS_Rear_Hole_1_Bottom
  AttacherType = Attacher::AttachEngine3D
  MapMode = 11
  Placement = pos=(-57.75,0,21.75) rot=(0.57735,-0.57735,0.57735;2.0944rad)
  Support = -> [Pocket]
FEATURE [PartDesign::CoordinateSystem] LCS_Rear_Hole_1_Top
  AttacherType = Attacher::AttachEngine3D
  MapMode = 11
  Placement = pos=(-57.75,-4,21.75) rot=(0.57735,-0.57735,0.57735;2.0944rad)
  Support = -> [Pocket002]
FEATURE [PartDesign::CoordinateSystem] LCS_Rear_Hole_2_Top
  AttacherType = Attacher::AttachEngine3D
  MapMode = 11
  Placement = pos=(57.75,-4,21.75) rot=(0.57735,-0.57735,0.57735;2.0944rad)
  Support = -> [Pocket]
FEATURE [PartDesign::CoordinateSystem] LCS_Rear_Hole_3_Top
  AttacherType = Attacher::AttachEngine3D
  MapMode = 11
  Placement = pos=(57.75,-4,-21.75) rot=(0.57735,-0.57735,0.57735;2.0944rad)
  Support = -> [Pocket]
FEATURE [PartDesign::CoordinateSystem] LCS_Rear_Hole_4_Top
  AttacherType = Attacher::AttachEngine3D
  MapMode = 11
  Placement = pos=(-57.75,-4,-21.75) rot=(0.57735,-0.57735,0.57735;2.0944rad)
  Support = -> [Pocket]
FEATURE [PartDesign::CoordinateSystem] LCS_Rear_Holder_Connector
  AttacherType = Attacher::AttachEngine3D
  MapMode = 11
  Placement = pos=(-47.5,-2,-15) rot=(0.57735,-0.57735,0.57735;2.0944rad)
  Support = -> [Pocket]
FEATURE [PartDesign::CoordinateSystem] LCS_Rear_STlink_Connector
  AttacherType = Attacher::AttachEngine3D
  MapMode = 11
  Placement = pos=(-47.5,-2,15) rot=(0.57735,-0.57735,0.57735;2.0944rad)
  Support = -> [Pocket]
FEATURE [PartDesign::CoordinateSystem] LCS_Rear_IDC_Connector  label="LCS_Rear_IEC_Connector"
  AttacherType = Attacher::AttachEngine3D
  MapMode = 11
  Placement = pos=(10,-4,-10) rot=(0.57735,-0.57735,0.57735;2.0944rad)
  Support = -> [Pocket]
FEATURE [PartDesign::CoordinateSystem] LCS_Rear_Switch
  AttacherType = Attacher::AttachEngine3D
  MapMode = 45
  Placement = pos=(30,-4,13) rot=(-0.57735,-0.57735,-0.57735;2.0944rad)
  Support = -> [Pocket]
FEATURE [PartDesign::Body] Body001  label="Rear_Panel"
  Group = -> [Sketch003,Pad001,Sketch004,Hole001,Sketch005,Pocket,LCS_Rear_Hole_1_Bottom,LCS_Rear_Hole_1_Top,LCS_Rear_Hole_2_Top,LCS_Rear_Hole_3_Top,LCS_Rear_Hole_4_Top,LCS_Rear_Switch,LCS_Rear_IDC_Connector,LCS_Rear_STlink_Connector,LCS_Rear_Holder_Connector,Sketch006,ShapeString,Pocket001,ShapeString001,Pocket002]
  Origin = -> Origin001
  Placement = pos=(0,0,-70) rot=(0,0,1;0rad)
  Tip = -> Pocket002
FEATURE [PartDesign::CoordinateSystem] LCS_Front_Connector_Hole_1
  AttacherType = Attacher::AttachEngine3D
  MapMode = 11
  Placement = pos=(-47.25,-4,7.25) rot=(0.57735,-0.57735,0.57735;2.0944rad)
  Support = -> [Fillet]
FEATURE [PartDesign::CoordinateSystem] LCS_Front_Connector_Hole_2
  AttacherType = Attacher::AttachEngine3D
  MapMode = 11
  Placement = pos=(-32.75,-4,7.25) rot=(0.57735,-0.57735,0.57735;2.0944rad)
  Support = -> [Fillet]
FEATURE [PartDesign::CoordinateSystem] LCS_Front_Connector_Hole_3
  AttacherType = Attacher::AttachEngine3D
  MapMode = 11
  Placement = pos=(-32.75,-4,-7.25) rot=(0.57735,-0.57735,0.57735;2.0944rad)
  Support = -> [Fillet]
FEATURE [PartDesign::CoordinateSystem] LCS_Front_Connector_Hole_4
  AttacherType = Attacher::AttachEngine3D
  MapMode = 11
  Placement = pos=(-47.25,-4,-7.25) rot=(0.57735,-0.57735,0.57735;2.0944rad)
  Support = -> [Fillet]
FEATURE [PartDesign::Body] Body  label="Front_Panel"
  Group = -> [Sketch001,Sketch,Pad,Sketch002,Hole,Chamfer,Fillet,LCS_PCBA_Mount,LCS_Front_Hole_1_Bottom,LCS_Front_Hole_1_Top,LCS_Front_Hole_2_Top,LCS_Front_Hole_3_Top,LCS_Front_Hole_4_Top,LCS_Front_Connector_Hole_1,LCS_Front_Connector_Hole_2,LCS_Front_Connector_Hole_3,LCS_Front_Connector_Hole_4]
  Origin = -> Origin
  Tip = -> Fillet
note: 2 file-system paths scrubbed to <path> (originals preserved in the JSON sidecar)
---- part Parts/Transformer.FCStd = doc fcstd_972766ebd56b ----
FCSTD DOCUMENT  (FreeCAD 0.20R28730 (Git))
Label: Transformer
License: All rights reserved
LicenseURL: http://en.wikipedia.org/wiki/All_rights_reserved
objects: PartDesign::CoordinateSystem×7, Sketcher::SketchObject×5, PartDesign::Revolution×3, PartDesign::Body×3, PartDesign::AdditivePipe×1
note: 23 computed .brp shape members not serialized (recipe doc carries the construction recipe); baked Part::Feature solids carry a one-line shape summary decoded from their .brp

FEATURE [Sketcher::SketchObject] Sketch
  FullyConstrained = true
  MapMode = 5
  Placement = pos=(0,0,0) rot=(1,0,0;1.5708rad)
  Support = -> [XZ_Plane]
  sketch-geometry (10):
    g0: ArcOfCircle CenterX=29 CenterY=33.5 CenterZ=0 NormalX=0 NormalY=0 NormalZ=1 AngleXU=0 Radius=12 StartAngle=1.5708 EndAngle=3.14159
    g1: LineSegment StartX=29 StartY=45.5 StartZ=0 EndX=40.5 EndY=45.5 EndZ=0
    g2: ArcOfCircle CenterX=40.5 CenterY=33.5 CenterZ=0 NormalX=0 NormalY=0 NormalZ=1 AngleXU=0 Radius=12 StartAngle=2e-16 EndAngle=1.5708
    g3: LineSegment StartX=52.5 StartY=33.5 StartZ=0 EndX=52.5 EndY=12.5 EndZ=0
    g4: ArcOfCircle CenterX=40.5 CenterY=12.5 CenterZ=0 NormalX=0 NormalY=0 NormalZ=1 AngleXU=0 Radius=12 StartAngle=4.71239 EndAngle=6.28319
    g5: LineSegment StartX=40.5 StartY=0.5 StartZ=0 EndX=29 EndY=0.5 EndZ=0
    g6: ArcOfCircle CenterX=29 CenterY=12.5 CenterZ=0 NormalX=0 NormalY=0 NormalZ=1 AngleXU=0 Radius=12 StartAngle=3.14159 EndAngle=4.71239
    g7: LineSegment StartX=17 StartY=12.5 StartZ=0 EndX=17 EndY=33.5 EndZ=0
    g8: GeomPoint X=17 Y=45.5 Z=0
    g9: GeomPoint X=52.5 Y=0.5 Z=0
  constraints (24):
    c: Tangent(g0,g1) = 1.5708
    c: Tangent(g1,g2) = 1.5708
    c: Tangent(g2,g3) = 1.5708
    c: Tangent(g3,g4) = 1.5708
    c: Tangent(g4,g5) = 1.5708
    c: Tangent(g5,g6) = 1.5708
    c: Tangent(g6,g7) = 1.5708
    c: Tangent(g7,g0) = 1.5708
    c: Horizontal(g1)
    c: Horizontal(g5)
    c: Vertical(g3)
    c: Vertical(g7)
    c: Equal(g0,g2)
    c: Equal(g2,g4)
    c: Equal(g4,g6)
    c: PointOnObject(g8,g1)
    c: PointOnObject(g8,g7)
    c: PointOnObject(g9,g3)
    c: PointOnObject(g9,g5)
    c: Radius(g4) = 12
    c: DistanceY(g5,g0) = 45
    c: DistanceY(g-1,g5) = 0.5
    c: DistanceX(g-1,g6) = 17
    c: DistanceX(g-1,g3) = 52.5
FEATURE [PartDesign::Revolution] Revolution
  Angle = 360
  Axis = (0,-2e-16,1)
  Base = (0,0,0)
  Placement = pos=(0,0,0) rot=(1,0,0;1.5708rad)
  Profile = -> Sketch
  ReferenceAxis = -> Sketch [V_Axis]
  Refine = true
  Reversed = true
FEATURE [Sketcher::SketchObject] Sketch001
  FullyConstrained = true
  MapMode = 5
  Placement = pos=(0,0,0) rot=(1,0,0;1.5708rad)
  Support = -> [XZ_Plane]
  sketch-geometry (2):
    g0: ArcOfCircle CenterX=-40 CenterY=55 CenterZ=0 NormalX=0 NormalY=0 NormalZ=1 AngleXU=0 Radius=15 StartAngle=4.14985 EndAngle=4.71239
    g1: ArcOfCircle CenterX=-55 CenterY=31.2089 CenterZ=0 NormalX=0 NormalY=0 NormalZ=1 AngleXU=0 Radius=13.125 StartAngle=1.00826 EndAngle=2.75077
  constraints (8):
    c: DistanceX(g0,g-1) = 40
    c: DistanceY(g-1,g0) = 40
    c: Vertical(g0,g0)
    c: Tangent(g1,g0) = 1.5708
    c: Radius(g0) = 15
    c: DistanceX(g0,g0) = 8
    c: DistanceX(g1,g0) = 15
    c: DistanceY(g1,g1) = 5
FEATURE [Sketcher::SketchObject] Sketch002
  AttachmentOffset = pos=(0,0,-40) rot=(0,0,1;0rad)
  FullyConstrained = true
  MapMode = 5
  Placement = pos=(-40,8.9e-15,-8.9e-15) rot=(0.57735,0.57735,0.57735;2.0944rad)
  Support = -> [YZ_Plane]
  sketch-geometry (4):
    g0: ArcOfCircle CenterX=-4 CenterY=40 CenterZ=0 NormalX=0 NormalY=0 NormalZ=1 AngleXU=0 Radius=2 StartAngle=1.5708 EndAngle=4.71239
    g1: ArcOfCircle CenterX=4 CenterY=40 CenterZ=0 NormalX=0 NormalY=0 NormalZ=1 AngleXU=0 Radius=2 StartAngle=4.71239 EndAngle=7.85398
    g2: LineSegment StartX=-4 StartY=38 StartZ=0 EndX=4 EndY=38 EndZ=0
    g3: LineSegment StartX=4 StartY=42 StartZ=0 EndX=-4 EndY=42 EndZ=0
  constraints (9):
    c: Tangent(g0,g2) = -1.5708
    c: Tangent(g2,g1) = -1.5708
    c: Tangent(g1,g3) = -1.5708
    c: Tangent(g3,g0) = -1.5708
    c: Equal(g0,g1)
    c: Symmetric(g0,g1,g-2)
    c: DistanceX(g2,g2) = 8
    c: DistanceY(g0,g0) = 4
    c: DistanceY(g-1,g0) = 40
FEATURE [PartDesign::AdditivePipe] AdditivePipe
  AuxilleryCurvelinear = true
  AuxillerySpineTangent = false
  BaseFeature = -> Revolution
  Binormal = (0,0,0)
  Mode = 0
  Placement = pos=(0,0,0) rot=(1,0,0;1.5708rad)
  Profile = -> Sketch002
  Refine = true
  Spine = -> Sketch001
  SpineTangent = false
  Transformation = 0
  Transition = 0
FEATURE [Sketcher::SketchObject] Sketch003
  FullyConstrained = true
  MapMode = 5
  Placement = pos=(0,0,0) rot=(1,0,0;1.5708rad)
  Support = -> [XZ_Plane001]
  sketch-geometry (4):
    g0: LineSegment StartX=24 StartY=0 StartZ=0 EndX=46 EndY=0 EndZ=0
    g1: LineSegment StartX=46 StartY=0 StartZ=0 EndX=46 EndY=0.5 EndZ=0
    g2: LineSegment StartX=46 StartY=0.5 StartZ=0 EndX=24 EndY=0.5 EndZ=0
    g3: LineSegment StartX=24 StartY=0.5 StartZ=0 EndX=24 EndY=0 EndZ=0
  constraints (12):
    c: Coincident(g0,g1)
    c: Coincident(g1,g2)
    c: Coincident(g2,g3)
    c: Coincident(g3,g0)
    c: Horizontal(g0)
    c: Horizontal(g2)
    c: Vertical(g1)
    c: Vertical(g3)
    c: PointOnObject(g0,g-1)
    c: DistanceY(g3,g3) = 0.5
    c: DistanceX(g-1,g0) = 24
    c: DistanceX(g2,g2) = 22
FEATURE [PartDesign::Revolution] Revolution001
  Angle = 360
  Axis = (0,2e-16,1)
  Base = (0,0,0)
  Placement = pos=(0,0,0) rot=(1,0,0;1.5708rad)
  Profile = -> Sketch003
  ReferenceAxis = -> Sketch003 [V_Axis]
  Refine = true
  Reversed = true
FEATURE [Sketcher::SketchObject] Sketch004
  FullyConstrained = true
  MapMode = 5
  Placement = pos=(0,0,0) rot=(1,0,0;1.5708rad)
  Support = -> [XZ_Plane002]
  sketch-geometry (8):
    g0: LineSegment StartX=45 StartY=6.5 StartZ=0 EndX=20.4569 EndY=6.5 EndZ=0
    g1: LineSegment StartX=20.4569 StartY=6.5 StartZ=0 EndX=14.4569 EndY=1.5 EndZ=0
    g2: LineSegment StartX=14.4569 StartY=1.5 StartZ=0 EndX=3 EndY=1.5 EndZ=0
    g3: LineSegment StartX=3 StartY=1.5 StartZ=0 EndX=3 EndY=0 EndZ=0
    g4: LineSegment StartX=3 StartY=0 StartZ=0 EndX=15 EndY=0 EndZ=0
    g5: LineSegment StartX=15 StartY=0 StartZ=0 EndX=21 EndY=5 EndZ=0
    g6: LineSegment StartX=21 StartY=5 StartZ=0 EndX=45 EndY=5 EndZ=0
    g7: LineSegment StartX=45 StartY=5 StartZ=0 EndX=45 EndY=6.5 EndZ=0
  constraints (24):
    c: Horizontal(g0)
    c: Coincident(g0,g1)
    c: Coincident(g1,g2)
    c: Horizontal(g2)
    c: Coincident(g2,g3)
    c: Vertical(g3)
    c: Coincident(g3,g4)
    c: Horizontal(g4)
    c: Coincident(g4,g5)
    c: Coincident(g5,g6)
    c: Horizontal(g6)
    c: Coincident(g6,g7)
    c: Coincident(g7,g0)
    c: Vertical(g7)
    c: Parallel(g5,g1)
    c: Equal(g3,g7)
    c: DistanceY(g3,g3) = 1.5
    c: DistanceX(g-1,g2) = 3
    c: DistanceX(g-1,g0) = 45
    c: DistanceY(g2,g0) = 5
    c: DistanceX(g4,g4) = 12
    c: DistanceX(g6,g6) = 24
    c: Horizontal(g3,g-1)
    c: Distance(g1,g5) = 1.5
FEATURE [PartDesign::Revolution] Revolution002
  Angle = 360
  Axis = (0,2e-16,1)
  Base = (0,0,0)
  Placement = pos=(0,0,0) rot=(1,0,0;1.5708rad)
  Profile = -> Sketch004
  ReferenceAxis = -> Sketch004 [V_Axis]
  Refine = true
  Reversed = true
FEATURE [PartDesign::CoordinateSystem] LCS_Transformer_Top
  AttacherType = Attacher::AttachEngine3D
  MapMode = 11
  Placement = pos=(-3.6e-15,0,45.5) rot=(0.707107,-0.707107,0;3.14159rad)
  Support = -> [AdditivePipe]
FEATURE [PartDesign::CoordinateSystem] LCS_Transformer_Bottom
  AttacherType = Attacher::AttachEngine3D
  MapMode = 11
  Placement = pos=(-3.6e-15,0,0.5) rot=(0.707107,-0.707107,0;3.14159rad)
  Support = -> [AdditivePipe]
FEATURE [PartDesign::Body] Body  label="Transformer"
  Group = -> [Sketch,Revolution,Sketch001,Sketch002,AdditivePipe,LCS_Transformer_Top,LCS_Transformer_Bottom]
  Origin = -> Origin
  Tip = -> AdditivePipe
FEATURE [PartDesign::CoordinateSystem] LCS_Foam_Top
  AttacherType = Attacher::AttachEngine3D
  MapMode = 11
  Placement = pos=(0,2e-16,0.5) rot=(0.707107,-0.707107,0;3.14159rad)
  Support = -> [Revolution001]
FEATURE [PartDesign::CoordinateSystem] LCS_Foam_Bottom
  AttacherType = Attacher::AttachEngine3D
  MapMode = 11
  Placement = pos=(0,0,0) rot=(0.707107,-0.707107,0;3.14159rad)
  Support = -> [Revolution001]
FEATURE [PartDesign::Body] Body001  label="Foam"
  Group = -> [Sketch003,Revolution001,LCS_Foam_Top,LCS_Foam_Bottom]
  Origin = -> Origin001
  Placement = pos=(0,0,45) rot=(0,0,1;0rad)
  Tip = -> Revolution001
FEATURE [PartDesign::CoordinateSystem] LCS_Transformer_Washer_Plane
  AttacherType = Attacher::AttachEngine3D
  MapMode = 11
  Placement = pos=(0,2.2e-15,5) rot=(0.707107,-0.707107,0;3.14159rad)
  Support = -> [Revolution002]
FEATURE [PartDesign::CoordinateSystem] LCS_Transformer_Washer_Screw_Top
  AttacherType = Attacher::AttachEngine3D
  MapMode = 11
  Placement = pos=(0,7e-16,1.5) rot=(0.707107,-0.707107,0;3.14159rad)
  Support = -> [Revolution002]
FEATURE [PartDesign::CoordinateSystem] LCS_Transformer_Washer_Screw_Bottom
  AttacherType = Attacher::AttachEngine3D
  MapMode = 11
  Placement = pos=(0,0,0) rot=(0.707107,-0.707107,0;3.14159rad)
  Support = -> [Revolution002]
FEATURE [PartDesign::Body] Body002  label="Transformer_Washer"
  Group = -> [Sketch004,Revolution002,LCS_Transformer_Washer_Plane,LCS_Transformer_Washer_Screw_Top,LCS_Transformer_Washer_Screw_Bottom]
  Origin = -> Origin002
  Placement = pos=(0,0,40.5) rot=(0,0,1;0rad)
  Tip = -> Revolution002
